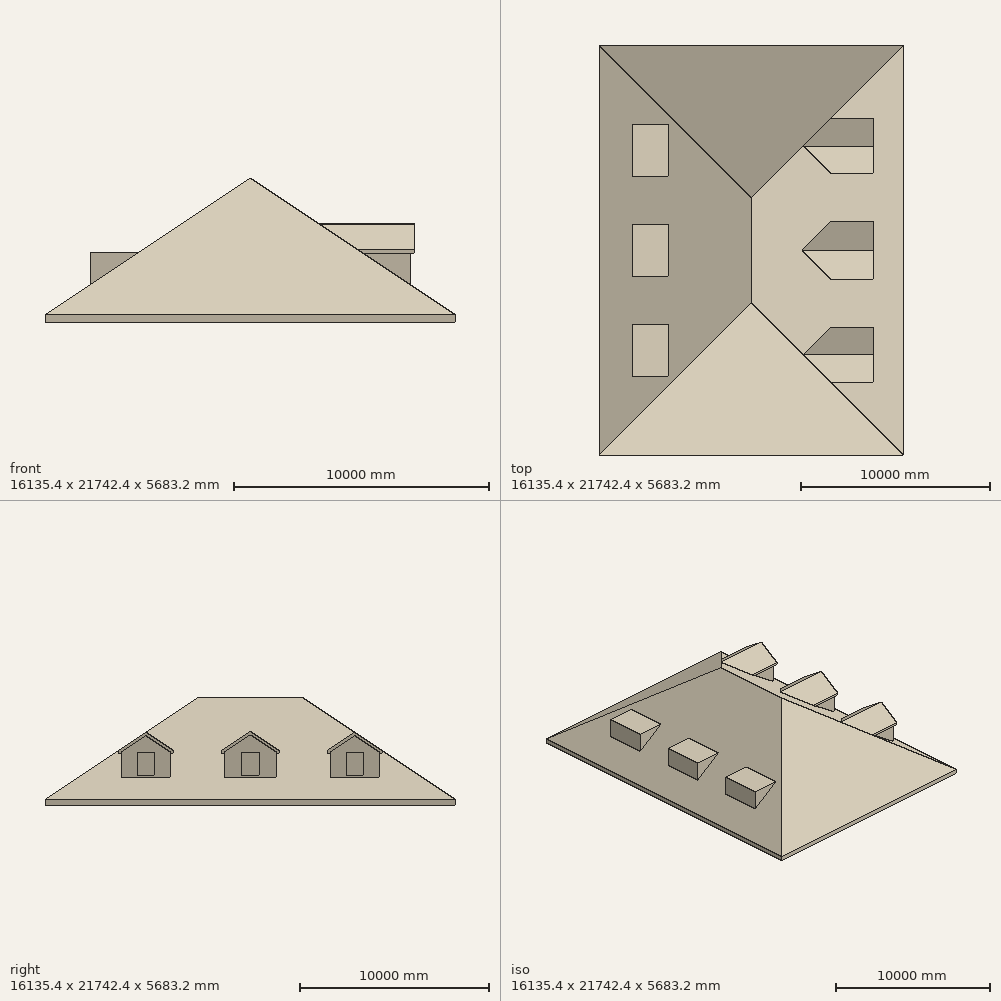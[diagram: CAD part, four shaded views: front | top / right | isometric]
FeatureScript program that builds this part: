
annotation { "Feature Type Name" : "Feature", "Feature Type Description" : "" }
export const myFeature = defineFeature(function(context is Context, id is Id, definition is map)
    precondition{}
    {
        {
            var Q0;
            Q0=qCreatedBy(makeId("Top.planeOp"),FACE);
            var sketch = newSketch(context, id + "F0", { "sketchPlane" : qUnion([Q0])});
            skLineSegment(sketch, "E0.bottom", {"start": v(0, 0) * mm, "end": v(15525.75, 0) * mm, "construction": true});
            skLineSegment(sketch, "E0.right", {"start": v(15525.75, 0) * mm, "end": v(15525.75, -21132.8) * mm, "construction": true});
            skLineSegment(sketch, "E1", {"start": v(13696.95, -21132.8) * mm, "end": v(13696.95, -22047.2) * mm, "construction": true});
            skLineSegment(sketch, "E2", {"start": v(13696.95, -22047.2) * mm, "end": v(9429.75, -22047.2) * mm, "construction": true});
            skLineSegment(sketch, "E3", {"start": v(9429.75, -22047.2) * mm, "end": v(9429.75, -21437.6) * mm, "construction": true});
            skLineSegment(sketch, "E4", {"start": v(9429.75, -21437.6) * mm, "end": v(8058.15, -21437.6) * mm, "construction": true});
            skLineSegment(sketch, "E5", {"start": v(8058.15, -21437.6) * mm, "end": v(8058.15, -21132.8) * mm, "construction": true});
            skLineSegment(sketch, "E6.trimOffspring", {"start": v(13696.95, -21132.8) * mm, "end": v(15525.75, -21132.8) * mm, "construction": true});
            skLineSegment(sketch, "E7", {"start": v(7600.95, -21132.8) * mm, "end": v(7600.95, -21590) * mm});
            skLineSegment(sketch, "E8", {"start": v(7600.95, -21590) * mm, "end": v(6838.95, -21590) * mm});
            skLineSegment(sketch, "E9", {"start": v(4019.55, -21590) * mm, "end": v(4019.55, -21132.8) * mm});
            skLineSegment(sketch, "E10.trimOffspring", {"start": v(7600.95, -21132.8) * mm, "end": v(8058.15, -21132.8) * mm, "construction": true});
            skLineSegment(sketch, "E11", {"start": v(4781.55, -21590) * mm, "end": v(4781.55, -21285.2) * mm});
            skLineSegment(sketch, "E12", {"start": v(4781.55, -21285.2) * mm, "end": v(4324.35, -21285.2) * mm});
            skLineSegment(sketch, "E13", {"start": v(4324.35, -21285.2) * mm, "end": v(4324.35, -19964.4) * mm});
            skLineSegment(sketch, "E14", {"start": v(4324.35, -19964.4) * mm, "end": v(7296.15, -19964.4) * mm});
            skLineSegment(sketch, "E15", {"start": v(7296.15, -19964.4) * mm, "end": v(7296.15, -21285.2) * mm});
            skLineSegment(sketch, "E16", {"start": v(7296.15, -21285.2) * mm, "end": v(6838.95, -21285.2) * mm});
            skLineSegment(sketch, "E17", {"start": v(6838.95, -21285.2) * mm, "end": v(6838.95, -21590) * mm});
            skLineSegment(sketch, "E18.trimOffspring", {"start": v(4781.55, -21590) * mm, "end": v(4019.55, -21590) * mm});
            skLineSegment(sketch, "E19", {"start": v(4019.55, -19659.6) * mm, "end": v(7600.95, -19659.6) * mm});
            skLineSegment(sketch, "E20", {"start": v(7600.95, -19659.6) * mm, "end": v(7600.95, -21132.8) * mm});
            skLineSegment(sketch, "E21", {"start": v(4019.55, -13868.4) * mm, "end": v(7486.65, -13868.4) * mm});
            skLineSegment(sketch, "E22", {"start": v(3905.25, -13754.1) * mm, "end": v(7486.65, -13754.1) * mm});
            skLineSegment(sketch, "E23", {"start": v(7600.95, -19659.6) * mm, "end": v(7600.95, -15201.9) * mm});
            skLineSegment(sketch, "E24", {"start": v(7486.65, -19659.6) * mm, "end": v(7486.65, -13754.1) * mm});
            skLineSegment(sketch, "E25.top", {"start": v(0, -21132.8) * mm, "end": v(4019.55, -21132.8) * mm, "construction": true});
            skLineSegment(sketch, "E25.right", {"start": v(4019.55, -13868.4) * mm, "end": v(4019.55, -21132.8) * mm});
            skLineSegment(sketch, "E26", {"start": v(0, 0) * mm, "end": v(0, -21132.8) * mm, "construction": true});
            skLineSegment(sketch, "E27", {"start": v(-304.8, -21437.6) * mm, "end": v(-304.8, 304.8) * mm});
            skLineSegment(sketch, "E28", {"start": v(-304.8, 304.8) * mm, "end": v(15830.55, 304.8) * mm});
            skLineSegment(sketch, "E29", {"start": v(15830.55, 304.8) * mm, "end": v(15830.55, -21437.6) * mm});
            skLineSegment(sketch, "E30", {"start": v(15830.55, -21437.6) * mm, "end": v(-304.8, -21437.6) * mm});
            skLineSegment(sketch, "E31.top", {"start": v(2895.6, -18237.2) * mm, "end": v(3905.25, -18237.2) * mm, "construction": true});
            skLineSegment(sketch, "E31.left", {"start": v(2895.6, -2895.6) * mm, "end": v(2895.6, -17240.25) * mm});
            skLineSegment(sketch, "E31.right", {"start": v(12630.15, -2895.6) * mm, "end": v(12630.15, -18237.2) * mm});
            skLineSegment(sketch, "E32", {"start": v(8058.15, -21437.6) * mm, "end": v(13696.95, -21437.6) * mm, "construction": true});
            skLineSegment(sketch, "E33", {"start": v(11563.35, -22047.2) * mm, "end": v(11563.35, -21437.6) * mm, "construction": true});
            skLineSegment(sketch, "E34", {"start": v(10877.55, -21437.6) * mm, "end": v(10877.55, -18237.2) * mm, "construction": true});
            skLineSegment(sketch, "E35", {"start": v(3905.25, -13754.1) * mm, "end": v(3905.25, -18237.2) * mm});
            skLineSegment(sketch, "E36", {"start": v(2895.6, -14732) * mm, "end": v(1676.4, -14732) * mm});
            skLineSegment(sketch, "E37", {"start": v(1676.4, -14732) * mm, "end": v(1676.4, -17018) * mm});
            skLineSegment(sketch, "E38", {"start": v(1676.4, -17018) * mm, "end": v(2895.6, -17018) * mm});
            skLineSegment(sketch, "E39", {"start": v(2895.6, -14509.75) * mm, "end": v(1454.15, -14509.75) * mm});
            skLineSegment(sketch, "E40", {"start": v(1454.15, -14509.75) * mm, "end": v(1454.15, -17240.25) * mm});
            skLineSegment(sketch, "E41", {"start": v(1454.15, -17240.25) * mm, "end": v(2895.6, -17240.25) * mm});
            skLineSegment(sketch, "E42", {"start": v(2895.6, -11709.4) * mm, "end": v(1676.4, -11709.4) * mm});
            skLineSegment(sketch, "E43", {"start": v(1676.4, -11709.4) * mm, "end": v(1676.4, -9423.4) * mm});
            skLineSegment(sketch, "E44", {"start": v(1676.4, -9423.4) * mm, "end": v(2895.6, -9423.4) * mm});
            skLineSegment(sketch, "E45", {"start": v(2895.6, -9201.15) * mm, "end": v(1454.15, -9201.15) * mm});
            skLineSegment(sketch, "E46", {"start": v(1454.15, -9201.15) * mm, "end": v(1454.15, -11931.65) * mm});
            skLineSegment(sketch, "E47", {"start": v(1454.15, -11931.65) * mm, "end": v(2895.6, -11931.65) * mm});
            skLineSegment(sketch, "E48", {"start": v(2895.6, -4114.8) * mm, "end": v(1676.4, -4114.8) * mm});
            skLineSegment(sketch, "E49", {"start": v(1676.4, -4114.8) * mm, "end": v(1676.4, -6400.8) * mm});
            skLineSegment(sketch, "E50", {"start": v(1676.4, -6400.8) * mm, "end": v(2895.6, -6400.8) * mm});
            skLineSegment(sketch, "E51", {"start": v(2895.6, -3892.55) * mm, "end": v(1454.15, -3892.55) * mm});
            skLineSegment(sketch, "E52", {"start": v(1454.15, -3892.55) * mm, "end": v(1454.15, -6623.05) * mm});
            skLineSegment(sketch, "E53", {"start": v(1454.15, -6623.05) * mm, "end": v(2895.6, -6623.05) * mm});
            skLineSegment(sketch, "E54", {"start": v(2895.6, -6623.05) * mm, "end": v(2895.6, -9201.15) * mm});
            skLineSegment(sketch, "E55", {"start": v(2895.6, -14509.75) * mm, "end": v(2895.6, -11931.65) * mm});
            skLineSegment(sketch, "E56", {"start": v(3505.2, -1371.6) * mm, "end": v(6045.2, -1371.6) * mm});
            skLineSegment(sketch, "E57", {"start": v(6045.2, -1371.6) * mm, "end": v(6045.2, -2895.6) * mm});
            skLineSegment(sketch, "E58", {"start": v(9480.55, -2895.6) * mm, "end": v(9480.55, -1371.6) * mm});
            skLineSegment(sketch, "E59", {"start": v(9480.55, -1371.6) * mm, "end": v(12020.55, -1371.6) * mm});
            skLineSegment(sketch, "E60", {"start": v(12020.55, -1371.6) * mm, "end": v(12020.55, -2895.6) * mm});
            skLineSegment(sketch, "E61", {"start": v(3282.95, -2895.6) * mm, "end": v(3282.95, -1149.35) * mm});
            skLineSegment(sketch, "E62", {"start": v(3282.95, -1149.35) * mm, "end": v(6267.45, -1149.35) * mm});
            skLineSegment(sketch, "E63", {"start": v(6267.45, -1149.35) * mm, "end": v(6267.45, -2895.6) * mm});
            skLineSegment(sketch, "E64", {"start": v(9258.3, -2895.6) * mm, "end": v(9258.3, -1149.35) * mm});
            skLineSegment(sketch, "E65", {"start": v(9258.3, -1149.35) * mm, "end": v(12242.8, -1149.35) * mm});
            skLineSegment(sketch, "E66", {"start": v(12242.8, -1149.35) * mm, "end": v(12242.8, -2895.6) * mm});
            skLineSegment(sketch, "E67", {"start": v(6553.2, -2895.6) * mm, "end": v(6553.2, -12649.2) * mm});
            skLineSegment(sketch, "E68", {"start": v(6667.5, -2895.6) * mm, "end": v(6667.5, -12763.5) * mm});
            skLineSegment(sketch, "E69", {"start": v(12630.15, -15036.8) * mm, "end": v(13849.35, -15036.8) * mm});
            skLineSegment(sketch, "E70", {"start": v(13849.35, -15036.8) * mm, "end": v(13849.35, -17170.4) * mm});
            skLineSegment(sketch, "E71", {"start": v(13849.35, -17170.4) * mm, "end": v(12630.15, -17170.4) * mm});
            skLineSegment(sketch, "E72", {"start": v(12630.15, -17392.65) * mm, "end": v(14071.6, -17392.65) * mm});
            skLineSegment(sketch, "E73", {"start": v(14071.6, -17392.65) * mm, "end": v(14071.6, -14814.55) * mm});
            skLineSegment(sketch, "E74", {"start": v(14071.6, -14814.55) * mm, "end": v(12630.15, -14814.55) * mm});
            skLineSegment(sketch, "E75", {"start": v(12630.15, -9423.4) * mm, "end": v(13849.35, -9423.4) * mm});
            skLineSegment(sketch, "E76", {"start": v(13849.35, -9423.4) * mm, "end": v(13849.35, -11709.4) * mm});
            skLineSegment(sketch, "E77", {"start": v(13849.35, -11709.4) * mm, "end": v(12630.15, -11709.4) * mm});
            skLineSegment(sketch, "E78", {"start": v(12630.15, -11931.65) * mm, "end": v(14071.6, -11931.65) * mm});
            skLineSegment(sketch, "E79", {"start": v(14071.6, -11931.65) * mm, "end": v(14071.6, -9201.15) * mm});
            skLineSegment(sketch, "E80", {"start": v(14071.6, -9201.15) * mm, "end": v(12630.15, -9201.15) * mm});
            skLineSegment(sketch, "E81", {"start": v(12630.15, -3962.4) * mm, "end": v(13849.35, -3962.4) * mm});
            skLineSegment(sketch, "E82", {"start": v(13849.35, -3962.4) * mm, "end": v(13849.35, -6096) * mm});
            skLineSegment(sketch, "E83", {"start": v(13849.35, -6096) * mm, "end": v(12630.15, -6096) * mm});
            skLineSegment(sketch, "E84", {"start": v(12630.15, -6318.25) * mm, "end": v(14071.6, -6318.25) * mm});
            skLineSegment(sketch, "E85", {"start": v(14071.6, -6318.25) * mm, "end": v(14071.6, -3740.15) * mm});
            skLineSegment(sketch, "E86", {"start": v(14071.6, -3740.15) * mm, "end": v(12630.15, -3740.15) * mm});
            skLineSegment(sketch, "E87", {"start": v(14071.6, -6318.25) * mm, "end": v(14071.6, -9201.15) * mm, "construction": true});
            skLineSegment(sketch, "E88", {"start": v(14071.6, -14814.55) * mm, "end": v(14071.6, -11931.65) * mm, "construction": true});
            skLineSegment(sketch, "E89", {"start": v(8934.45, -14770.1) * mm, "end": v(12630.15, -14770.1) * mm});
            skLineSegment(sketch, "E90", {"start": v(8934.45, -14884.4) * mm, "end": v(12630.15, -14884.4) * mm});
            skLineSegment(sketch, "E91", {"start": v(9721.85, -12319) * mm, "end": v(12630.15, -12319) * mm});
            skLineSegment(sketch, "E92", {"start": v(9836.15, -12433.3) * mm, "end": v(12630.15, -12433.3) * mm});
            skLineSegment(sketch, "E93", {"start": v(8820.15, -15087.6) * mm, "end": v(8820.15, -12763.5) * mm});
            skLineSegment(sketch, "E94", {"start": v(7658.1, -9156.7) * mm, "end": v(12630.15, -9156.7) * mm});
            skLineSegment(sketch, "E95", {"start": v(11817.35, -13246.1) * mm, "end": v(11817.35, -14770.1) * mm});
            skLineSegment(sketch, "E96", {"start": v(7486.65, -15087.6) * mm, "end": v(5238.75, -15087.6) * mm});
            skLineSegment(sketch, "E97", {"start": v(5238.75, -15087.6) * mm, "end": v(5238.75, -18135.6) * mm});
            skLineSegment(sketch, "E98", {"start": v(5238.75, -18135.6) * mm, "end": v(4019.55, -18135.6) * mm});
            skLineSegment(sketch, "E99", {"start": v(2895.6, -2895.6) * mm, "end": v(12630.15, -2895.6) * mm});
            skLineSegment(sketch, "E100", {"start": v(3505.2, -1371.6) * mm, "end": v(3505.2, -2895.6) * mm});
            skLineSegment(sketch, "E101", {"start": v(6267.45, -2794) * mm, "end": v(9258.3, -2794) * mm});
            skLineSegment(sketch, "E102", {"start": v(2794, -3892.55) * mm, "end": v(2794, -2794) * mm});
            skLineSegment(sketch, "E103", {"start": v(2794, -2794) * mm, "end": v(3282.95, -2794) * mm});
            skLineSegment(sketch, "E104", {"start": v(2794, -6623.05) * mm, "end": v(2794, -9201.15) * mm});
            skLineSegment(sketch, "E105", {"start": v(2794, -11931.65) * mm, "end": v(2794, -14509.75) * mm});
            skLineSegment(sketch, "E106", {"start": v(2794, -17240.25) * mm, "end": v(2794, -18338.8) * mm, "construction": true});
            skLineSegment(sketch, "E107", {"start": v(2794, -18338.8) * mm, "end": v(4019.55, -18338.8) * mm, "construction": true});
            skLineSegment(sketch, "E108", {"start": v(7600.95, -18338.8) * mm, "end": v(12731.75, -18338.8) * mm});
            skLineSegment(sketch, "E109", {"start": v(12731.75, -18338.8) * mm, "end": v(12731.75, -17392.65) * mm});
            skLineSegment(sketch, "E110", {"start": v(12731.75, -14814.55) * mm, "end": v(12731.75, -11931.65) * mm});
            skLineSegment(sketch, "E111", {"start": v(12731.75, -9201.15) * mm, "end": v(12731.75, -6318.25) * mm});
            skLineSegment(sketch, "E112", {"start": v(12242.8, -2794) * mm, "end": v(12731.75, -2794) * mm});
            skLineSegment(sketch, "E113", {"start": v(12731.75, -2794) * mm, "end": v(12731.75, -3740.15) * mm});
            skLineSegment(sketch, "E114", {"start": v(6667.5, -12763.5) * mm, "end": v(2895.6, -12763.5) * mm});
            skLineSegment(sketch, "E115", {"start": v(6553.2, -12649.2) * mm, "end": v(2895.6, -12649.2) * mm});
            skLineSegment(sketch, "E116", {"start": v(7486.65, -15087.6) * mm, "end": v(8820.15, -15087.6) * mm});
            skLineSegment(sketch, "E117", {"start": v(7600.95, -15201.9) * mm, "end": v(8934.45, -15201.9) * mm});
            skLineSegment(sketch, "E118.trimOffspring", {"start": v(8934.45, -14884.4) * mm, "end": v(8934.45, -15201.9) * mm});
            skLineSegment(sketch, "E119", {"start": v(9721.85, -12319) * mm, "end": v(9721.85, -14770.1) * mm});
            skLineSegment(sketch, "E120", {"start": v(9836.15, -12433.3) * mm, "end": v(9836.15, -14770.1) * mm});
            skLineSegment(sketch, "E121", {"start": v(10445.75, -12433.3) * mm, "end": v(10445.75, -14770.1) * mm});
            skLineSegment(sketch, "E122", {"start": v(12630.15, -13246.1) * mm, "end": v(11715.75, -13246.1) * mm});
            skLineSegment(sketch, "E123", {"start": v(11715.75, -13246.1) * mm, "end": v(11715.75, -13131.8) * mm});
            skLineSegment(sketch, "E124", {"start": v(11715.75, -13131.8) * mm, "end": v(12630.15, -13131.8) * mm});
            skLineSegment(sketch, "E125.bottom", {"start": v(12350.75, -12534.9) * mm, "end": v(12579.35, -12534.9) * mm});
            skLineSegment(sketch, "E125.top", {"start": v(12350.75, -13042.9) * mm, "end": v(12579.35, -13042.9) * mm});
            skLineSegment(sketch, "E125.left", {"start": v(12350.75, -12534.9) * mm, "end": v(12350.75, -13042.9) * mm});
            skLineSegment(sketch, "E125.right", {"start": v(12579.35, -12534.9) * mm, "end": v(12579.35, -13042.9) * mm});
            skLineSegment(sketch, "E126", {"start": v(12350.75, -12636.5) * mm, "end": v(11855.45, -12636.5) * mm});
            skLineSegment(sketch, "E127", {"start": v(11855.45, -12636.5) * mm, "end": v(11855.45, -12941.3) * mm});
            skLineSegment(sketch, "E128", {"start": v(11855.45, -12941.3) * mm, "end": v(12350.75, -12941.3) * mm});
            skLineSegment(sketch, "E129", {"start": v(11004.55, -14770.1) * mm, "end": v(11004.55, -14884.4) * mm});
            skLineSegment(sketch, "E130", {"start": v(11614.15, -14770.1) * mm, "end": v(11614.15, -14884.4) * mm});
            skLineSegment(sketch, "E131", {"start": v(11004.55, -14827.25) * mm, "end": v(11614.15, -14827.25) * mm});
            skCircle(sketch, "E132", {"center": v(10140.95, -13195.3) * mm, "radius": 165.1 * mm});
            skLineSegment(sketch, "E133", {"start": v(9836.15, -13500.1) * mm, "end": v(10445.75, -13500.1) * mm, "construction": true});
            skLineSegment(sketch, "E134", {"start": v(10445.75, -12890.5) * mm, "end": v(9836.15, -12890.5) * mm});
            skLineSegment(sketch, "E135", {"start": v(11004.55, -12319) * mm, "end": v(11004.55, -12433.3) * mm});
            skLineSegment(sketch, "E136", {"start": v(11614.15, -12319) * mm, "end": v(11614.15, -12433.3) * mm});
            skLineSegment(sketch, "E137", {"start": v(11004.55, -12376.15) * mm, "end": v(11614.15, -12376.15) * mm});
            skLineSegment(sketch, "E138.bottom", {"start": v(9112.25, -14465.3) * mm, "end": v(9620.25, -14465.3) * mm});
            skLineSegment(sketch, "E138.top", {"start": v(9112.25, -14719.3) * mm, "end": v(9620.25, -14719.3) * mm});
            skLineSegment(sketch, "E138.left", {"start": v(9112.25, -14465.3) * mm, "end": v(9112.25, -14719.3) * mm});
            skLineSegment(sketch, "E138.right", {"start": v(9620.25, -14465.3) * mm, "end": v(9620.25, -14719.3) * mm});
            skLineSegment(sketch, "E139.bottom", {"start": v(9213.85, -13970) * mm, "end": v(9518.65, -13970) * mm});
            skLineSegment(sketch, "E139.top", {"start": v(9213.85, -14465.3) * mm, "end": v(9518.65, -14465.3) * mm});
            skLineSegment(sketch, "E139.left", {"start": v(9213.85, -13970) * mm, "end": v(9213.85, -14465.3) * mm});
            skLineSegment(sketch, "E139.right", {"start": v(9518.65, -13970) * mm, "end": v(9518.65, -14465.3) * mm});
            skLineSegment(sketch, "E140", {"start": v(8934.45, -13220.7) * mm, "end": v(9721.85, -13220.7) * mm});
            skLineSegment(sketch, "E141", {"start": v(8934.45, -12763.5) * mm, "end": v(9721.85, -12763.5) * mm});
            skLineSegment(sketch, "E142", {"start": v(7702.55, -15087.6) * mm, "end": v(7702.55, -15201.9) * mm});
            skLineSegment(sketch, "E143", {"start": v(8616.95, -15087.6) * mm, "end": v(8616.95, -15201.9) * mm});
            skLineSegment(sketch, "E144", {"start": v(7702.55, -15144.75) * mm, "end": v(8616.95, -15144.75) * mm});
            skLineSegment(sketch, "E145", {"start": v(8820.15, -13322.3) * mm, "end": v(8934.45, -13322.3) * mm});
            skLineSegment(sketch, "E146", {"start": v(8820.15, -13931.9) * mm, "end": v(8934.45, -13931.9) * mm});
            skLineSegment(sketch, "E147", {"start": v(8877.3, -13931.9) * mm, "end": v(8877.3, -13322.3) * mm});
            skCircle(sketch, "E148", {"center": v(9264.65, -12992.1) * mm, "radius": 165.1 * mm});
            skLineSegment(sketch, "E149", {"start": v(7658.1, -12763.5) * mm, "end": v(8820.15, -12763.5) * mm});
            skLineSegment(sketch, "E150", {"start": v(7658.1, -12763.5) * mm, "end": v(7658.1, -9156.7) * mm});
            skLineSegment(sketch, "E151.trimOffspring", {"start": v(8934.45, -12763.5) * mm, "end": v(8934.45, -14770.1) * mm});
            skLineSegment(sketch, "E152", {"start": v(9721.85, -12649.2) * mm, "end": v(7772.4, -12649.2) * mm});
            skLineSegment(sketch, "E153", {"start": v(7772.4, -12649.2) * mm, "end": v(7772.4, -9271) * mm});
            skLineSegment(sketch, "E154", {"start": v(7772.4, -9271) * mm, "end": v(12630.15, -9271) * mm});
            skLineSegment(sketch, "E155", {"start": v(8737.6, -12763.5) * mm, "end": v(8737.6, -12649.2) * mm});
            skLineSegment(sketch, "E156", {"start": v(7874, -12763.5) * mm, "end": v(7874, -12649.2) * mm});
            skLineSegment(sketch, "E157", {"start": v(7874, -12706.35) * mm, "end": v(8737.6, -12706.35) * mm});
            skLineSegment(sketch, "E158", {"start": v(7772.4, -11734.8) * mm, "end": v(8496.3, -11734.8) * mm});
            skLineSegment(sketch, "E159", {"start": v(9105.9, -11125.2) * mm, "end": v(9105.9, -9271) * mm});
            skLineSegment(sketch, "E160", {"start": v(7772.4, -11620.5) * mm, "end": v(8448.96, -11620.5) * mm});
            skLineSegment(sketch, "E161", {"start": v(8991.6, -11077.86) * mm, "end": v(8991.6, -9271) * mm});
            skLineSegment(sketch, "E162", {"start": v(8280.4, -9271) * mm, "end": v(8280.4, -11620.5) * mm});
            skLineSegment(sketch, "E163", {"start": v(5334, -12649.2) * mm, "end": v(5334, -6553.2) * mm, "construction": true});
            skLineSegment(sketch, "E164", {"start": v(5334, -6553.2) * mm, "end": v(6667.5, -6553.2) * mm, "construction": true});
            skLineSegment(sketch, "E165", {"start": v(2895.6, -17018) * mm, "end": v(3905.25, -17018) * mm});
            skLineSegment(sketch, "E166", {"start": v(2895.6, -17132.3) * mm, "end": v(3905.25, -17132.3) * mm});
            skLineSegment(sketch, "E167", {"start": v(8991.6, -9779) * mm, "end": v(8280.4, -9779) * mm});
            skLineSegment(sketch, "E168", {"start": v(8448.96, -11620.5) * mm, "end": v(8991.6, -11077.86) * mm});
            skLineSegment(sketch, "E169", {"start": v(8496.3, -11734.8) * mm, "end": v(9105.9, -11125.2) * mm});
            skLineSegment(sketch, "E170", {"start": v(8515.65, -11553.8) * mm, "end": v(8596.47, -11634.63) * mm});
            skLineSegment(sketch, "E171", {"start": v(8946.7, -11122.76) * mm, "end": v(9027.52, -11203.58) * mm});
            skLineSegment(sketch, "E172", {"start": v(8556.06, -11594.22) * mm, "end": v(8987.1, -11163.17) * mm});
            skLineSegment(sketch, "E173", {"start": v(6667.5, -8699.5) * mm, "end": v(7658.1, -8699.5) * mm});
            skLineSegment(sketch, "E174", {"start": v(6667.5, -8813.8) * mm, "end": v(7658.1, -8813.8) * mm});
            skLineSegment(sketch, "E175", {"start": v(6731, -8699.5) * mm, "end": v(6731, -8813.8) * mm});
            skLineSegment(sketch, "E176", {"start": v(7594.6, -8699.5) * mm, "end": v(7594.6, -8813.8) * mm});
            skLineSegment(sketch, "E177", {"start": v(6731, -8756.65) * mm, "end": v(7594.6, -8756.65) * mm});
            skLineSegment(sketch, "E178", {"start": v(13849.35, -15570.2) * mm, "end": v(14071.6, -15570.2) * mm});
            skLineSegment(sketch, "E179", {"start": v(13849.35, -16789.4) * mm, "end": v(14071.6, -16789.4) * mm});
            skLineSegment(sketch, "E180", {"start": v(13960.47, -16789.4) * mm, "end": v(13960.47, -15570.2) * mm});
            skLineSegment(sketch, "E181", {"start": v(13849.35, -9956.8) * mm, "end": v(14071.6, -9956.8) * mm});
            skLineSegment(sketch, "E182", {"start": v(13849.35, -11176) * mm, "end": v(14071.6, -11176) * mm});
            skLineSegment(sketch, "E183", {"start": v(13960.47, -11176) * mm, "end": v(13960.47, -9956.8) * mm});
            skLineSegment(sketch, "E184", {"start": v(13849.35, -4343.4) * mm, "end": v(14071.6, -4343.4) * mm});
            skLineSegment(sketch, "E185", {"start": v(13849.35, -5562.6) * mm, "end": v(14071.6, -5562.6) * mm});
            skLineSegment(sketch, "E186", {"start": v(13960.47, -4343.4) * mm, "end": v(13960.47, -5562.6) * mm});
            skLineSegment(sketch, "E187", {"start": v(9734.55, -1149.35) * mm, "end": v(9734.55, -1371.6) * mm});
            skLineSegment(sketch, "E188", {"start": v(10648.95, -1149.35) * mm, "end": v(10648.95, -1371.6) * mm});
            skLineSegment(sketch, "E189", {"start": v(9734.55, -1260.47) * mm, "end": v(10648.95, -1260.47) * mm});
            skLineSegment(sketch, "E190", {"start": v(10852.15, -1149.35) * mm, "end": v(10852.15, -1371.6) * mm});
            skLineSegment(sketch, "E191", {"start": v(11766.55, -1149.35) * mm, "end": v(11766.55, -1371.6) * mm});
            skLineSegment(sketch, "E192", {"start": v(10852.15, -1260.47) * mm, "end": v(11766.55, -1260.47) * mm});
            skLineSegment(sketch, "E193", {"start": v(3759.2, -1371.6) * mm, "end": v(3759.2, -1149.35) * mm});
            skLineSegment(sketch, "E194", {"start": v(4673.6, -1371.6) * mm, "end": v(4673.6, -1149.35) * mm});
            skLineSegment(sketch, "E195", {"start": v(4876.8, -1371.6) * mm, "end": v(4876.8, -1149.35) * mm});
            skLineSegment(sketch, "E196", {"start": v(5791.2, -1371.6) * mm, "end": v(5791.2, -1149.35) * mm});
            skLineSegment(sketch, "E197", {"start": v(3759.2, -1260.47) * mm, "end": v(4673.6, -1260.47) * mm});
            skLineSegment(sketch, "E198", {"start": v(4876.8, -1260.47) * mm, "end": v(5791.2, -1260.47) * mm});
            skLineSegment(sketch, "E199", {"start": v(1454.15, -5867.4) * mm, "end": v(1676.4, -5867.4) * mm});
            skLineSegment(sketch, "E200", {"start": v(1454.15, -4648.2) * mm, "end": v(1676.4, -4648.2) * mm});
            skLineSegment(sketch, "E201", {"start": v(1565.27, -5867.4) * mm, "end": v(1565.27, -4648.2) * mm});
            skLineSegment(sketch, "E202", {"start": v(1454.15, -9956.8) * mm, "end": v(1676.4, -9956.8) * mm});
            skLineSegment(sketch, "E203", {"start": v(1454.15, -11176) * mm, "end": v(1676.4, -11176) * mm});
            skLineSegment(sketch, "E204", {"start": v(1565.27, -11176) * mm, "end": v(1565.27, -9956.8) * mm});
            skLineSegment(sketch, "E205", {"start": v(2895.6, -17240.25) * mm, "end": v(2895.6, -18237.2) * mm, "construction": true});
            skLineSegment(sketch, "E206", {"start": v(3905.25, -18237.2) * mm, "end": v(12630.15, -18237.2) * mm});
            skLineSegment(sketch, "E207", {"start": v(1454.15, -15265.4) * mm, "end": v(1676.4, -15265.4) * mm});
            skLineSegment(sketch, "E208", {"start": v(1454.15, -16484.6) * mm, "end": v(1676.4, -16484.6) * mm});
            skLineSegment(sketch, "E209", {"start": v(1565.27, -16484.6) * mm, "end": v(1565.27, -15265.4) * mm});
            skLineSegment(sketch, "E210", {"start": v(9734.55, -18338.8) * mm, "end": v(9734.55, -21437.6) * mm});
            skLineSegment(sketch, "E211", {"start": v(9620.25, -18338.8) * mm, "end": v(9620.25, -21437.6) * mm});
            skLineSegment(sketch, "E212", {"start": v(12020.55, -18338.8) * mm, "end": v(12020.55, -21437.6) * mm});
            skLineSegment(sketch, "E213", {"start": v(12134.85, -18338.8) * mm, "end": v(12134.85, -21437.6) * mm});
            skLineSegment(sketch, "E214", {"start": v(10242.55, -18338.8) * mm, "end": v(10242.55, -21437.6) * mm});
            skLineSegment(sketch, "E215", {"start": v(11512.55, -18338.8) * mm, "end": v(11512.55, -21437.6) * mm});
            skLineSegment(sketch, "E216", {"start": v(10572.75, -18237.2) * mm, "end": v(10572.75, -18338.8) * mm});
            skLineSegment(sketch, "E217", {"start": v(11182.35, -18237.2) * mm, "end": v(11182.35, -18338.8) * mm});
            skLineSegment(sketch, "E218", {"start": v(10572.75, -18288) * mm, "end": v(11182.35, -18288) * mm});
            skLineSegment(sketch, "E219", {"start": v(7658.1, -9156.7) * mm, "end": v(7658.1, -6096) * mm});
            skLineSegment(sketch, "E220", {"start": v(7658.1, -6096) * mm, "end": v(12630.15, -6096) * mm});
            skLineSegment(sketch, "E221", {"start": v(7772.4, -9156.7) * mm, "end": v(7772.4, -6210.3) * mm});
            skLineSegment(sketch, "E222", {"start": v(7772.4, -6210.3) * mm, "end": v(12630.15, -6210.3) * mm});
            skLineSegment(sketch, "E223", {"start": v(9601.2, -9156.7) * mm, "end": v(9601.2, -8293.1) * mm});
            skLineSegment(sketch, "E224", {"start": v(9601.2, -8293.1) * mm, "end": v(9715.5, -8293.1) * mm});
            skLineSegment(sketch, "E225", {"start": v(9715.5, -8293.1) * mm, "end": v(9715.5, -9156.7) * mm});
            skLineSegment(sketch, "E226", {"start": v(7772.4, -8547.1) * mm, "end": v(9601.2, -8547.1) * mm});
            skLineSegment(sketch, "E227", {"start": v(9144, -8547.1) * mm, "end": v(9144, -9156.7) * mm});
            skCircle(sketch, "E228", {"center": v(8458.2, -8851.9) * mm, "radius": 165.1 * mm});
            skLineSegment(sketch, "E229.bottom", {"start": v(9817.1, -8877.3) * mm, "end": v(10325.1, -8877.3) * mm});
            skLineSegment(sketch, "E229.top", {"start": v(9817.1, -9105.9) * mm, "end": v(10325.1, -9105.9) * mm});
            skLineSegment(sketch, "E229.left", {"start": v(9817.1, -8877.3) * mm, "end": v(9817.1, -9105.9) * mm});
            skLineSegment(sketch, "E229.right", {"start": v(10325.1, -8877.3) * mm, "end": v(10325.1, -9105.9) * mm});
            skLineSegment(sketch, "E230", {"start": v(9918.7, -8877.3) * mm, "end": v(9918.7, -8382) * mm});
            skLineSegment(sketch, "E231", {"start": v(9918.7, -8382) * mm, "end": v(10223.5, -8382) * mm});
            skLineSegment(sketch, "E232", {"start": v(10223.5, -8382) * mm, "end": v(10223.5, -8877.3) * mm});
            skLineSegment(sketch, "E233", {"start": v(9677.4, -6210.3) * mm, "end": v(9677.4, -7543.8) * mm});
            skLineSegment(sketch, "E234", {"start": v(9677.4, -7543.8) * mm, "end": v(11125.2, -7543.8) * mm});
            skLineSegment(sketch, "E235", {"start": v(11125.2, -7543.8) * mm, "end": v(11125.2, -6210.3) * mm});
            skLineSegment(sketch, "E236", {"start": v(9677.4, -7429.5) * mm, "end": v(7772.4, -7429.5) * mm});
            skLineSegment(sketch, "E237", {"start": v(9791.7, -6210.3) * mm, "end": v(9791.7, -7429.5) * mm});
            skLineSegment(sketch, "E238", {"start": v(9791.7, -7429.5) * mm, "end": v(11010.9, -7429.5) * mm});
            skLineSegment(sketch, "E239", {"start": v(11010.9, -7429.5) * mm, "end": v(11010.9, -6210.3) * mm});
            skLineSegment(sketch, "E240", {"start": v(9791.7, -7429.5) * mm, "end": v(11010.9, -6210.3) * mm});
            skLineSegment(sketch, "E241", {"start": v(11010.9, -7429.5) * mm, "end": v(9791.7, -6210.3) * mm});
            skLineSegment(sketch, "E242.bottom", {"start": v(7899.4, -6337.3) * mm, "end": v(9550.4, -6337.3) * mm});
            skLineSegment(sketch, "E242.top", {"start": v(7899.4, -7302.5) * mm, "end": v(9550.4, -7302.5) * mm});
            skLineSegment(sketch, "E242.left", {"start": v(7899.4, -6337.3) * mm, "end": v(7899.4, -7302.5) * mm});
            skLineSegment(sketch, "E242.right", {"start": v(9550.4, -6337.3) * mm, "end": v(9550.4, -7302.5) * mm});
            skLineSegment(sketch, "E243", {"start": v(10426.7, -9156.7) * mm, "end": v(10426.7, -7543.8) * mm});
            skLineSegment(sketch, "E244", {"start": v(10541, -9156.7) * mm, "end": v(10541, -7543.8) * mm});
            skLineSegment(sketch, "E245", {"start": v(10426.7, -7645.4) * mm, "end": v(10541, -7645.4) * mm});
            skLineSegment(sketch, "E246", {"start": v(10426.7, -8255) * mm, "end": v(10541, -8255) * mm});
            skLineSegment(sketch, "E247", {"start": v(10483.85, -8255) * mm, "end": v(10483.85, -7645.4) * mm});
            skLineSegment(sketch, "E248", {"start": v(9842.5, -7429.5) * mm, "end": v(9842.5, -7543.8) * mm});
            skLineSegment(sketch, "E249", {"start": v(10375.9, -7429.5) * mm, "end": v(10375.9, -7543.8) * mm});
            skLineSegment(sketch, "E250", {"start": v(9842.5, -7486.65) * mm, "end": v(10375.9, -7486.65) * mm});
            skLineSegment(sketch, "E251", {"start": v(10541, -8648.7) * mm, "end": v(12122.15, -8648.7) * mm});
            skLineSegment(sketch, "E252", {"start": v(12122.15, -8648.7) * mm, "end": v(12122.15, -6718.3) * mm});
            skLineSegment(sketch, "E253", {"start": v(12122.15, -6718.3) * mm, "end": v(11125.2, -6718.3) * mm});
            skLineSegment(sketch, "E254", {"start": v(7658.1, -7683.5) * mm, "end": v(7772.4, -7683.5) * mm});
            skLineSegment(sketch, "E255", {"start": v(7658.1, -8293.1) * mm, "end": v(7772.4, -8293.1) * mm});
            skLineSegment(sketch, "E256", {"start": v(7715.25, -8293.1) * mm, "end": v(7715.25, -7683.5) * mm});
            skLineSegment(sketch, "E257", {"start": v(4838.7, -11925.3) * mm, "end": v(4838.7, -12649.2) * mm});
            skLineSegment(sketch, "E258", {"start": v(2895.6, -12039.6) * mm, "end": v(4724.4, -12039.6) * mm});
            skLineSegment(sketch, "E259", {"start": v(4724.4, -12039.6) * mm, "end": v(4724.4, -12649.2) * mm});
            skLineSegment(sketch, "E260", {"start": v(6553.2, -8775.7) * mm, "end": v(5829.3, -8775.7) * mm});
            skLineSegment(sketch, "E261", {"start": v(5829.3, -8775.7) * mm, "end": v(5829.3, -12649.2) * mm});
            skLineSegment(sketch, "E262", {"start": v(6553.2, -8890) * mm, "end": v(5943.6, -8890) * mm});
            skLineSegment(sketch, "E263", {"start": v(5943.6, -8890) * mm, "end": v(5943.6, -12649.2) * mm});
            skLineSegment(sketch, "E264", {"start": v(4838.7, -11925.3) * mm, "end": v(2895.6, -11925.3) * mm});
            skLineSegment(sketch, "E265", {"start": v(4902.2, -12649.2) * mm, "end": v(4902.2, -12763.5) * mm});
            skLineSegment(sketch, "E266", {"start": v(5765.8, -12649.2) * mm, "end": v(5765.8, -12763.5) * mm});
            skLineSegment(sketch, "E267", {"start": v(4902.2, -12706.35) * mm, "end": v(5765.8, -12706.35) * mm});
            skLineSegment(sketch, "E268", {"start": v(2997.2, -11925.3) * mm, "end": v(2997.2, -12039.6) * mm});
            skLineSegment(sketch, "E269", {"start": v(4622.8, -11925.3) * mm, "end": v(4622.8, -12039.6) * mm});
            skLineSegment(sketch, "E270", {"start": v(2997.2, -11982.45) * mm, "end": v(4622.8, -11982.45) * mm});
            skLineSegment(sketch, "E271", {"start": v(6553.2, -12547.6) * mm, "end": v(6667.5, -12547.6) * mm});
            skLineSegment(sketch, "E272", {"start": v(6553.2, -10922) * mm, "end": v(6667.5, -10922) * mm});
            skLineSegment(sketch, "E273", {"start": v(6610.35, -12547.6) * mm, "end": v(6610.35, -10922) * mm});
            skLineSegment(sketch, "E274", {"start": v(5943.6, -10820.4) * mm, "end": v(6553.2, -10820.4) * mm});
            skLineSegment(sketch, "E275", {"start": v(5943.6, -10706.1) * mm, "end": v(6553.2, -10706.1) * mm});
            skLineSegment(sketch, "E276", {"start": v(5829.3, -10617.2) * mm, "end": v(5943.6, -10617.2) * mm});
            skLineSegment(sketch, "E277", {"start": v(5829.3, -8991.6) * mm, "end": v(5943.6, -8991.6) * mm});
            skLineSegment(sketch, "E278", {"start": v(5886.45, -8991.6) * mm, "end": v(5886.45, -10617.2) * mm});
            skLineSegment(sketch, "E279", {"start": v(6667.5, -3302) * mm, "end": v(8902.7, -3302) * mm});
            skLineSegment(sketch, "E280", {"start": v(8902.7, -3302) * mm, "end": v(8902.7, -5334) * mm});
            skLineSegment(sketch, "E281", {"start": v(8902.7, -5334) * mm, "end": v(6667.5, -5334) * mm});
            skLineSegment(sketch, "E282", {"start": v(8902.7, -3810) * mm, "end": v(9309.1, -3810) * mm});
            skLineSegment(sketch, "E283", {"start": v(9309.1, -3810) * mm, "end": v(9309.1, -4826) * mm});
            skLineSegment(sketch, "E284", {"start": v(9309.1, -4826) * mm, "end": v(8902.7, -4826) * mm});
            skLineSegment(sketch, "E285", {"start": v(10623.55, -6096) * mm, "end": v(10623.55, -5410.2) * mm});
            skLineSegment(sketch, "E286", {"start": v(10623.55, -5410.2) * mm, "end": v(12020.55, -5410.2) * mm});
            skLineSegment(sketch, "E287", {"start": v(12020.55, -5410.2) * mm, "end": v(12020.55, -6096) * mm});
            skSolve(sketch);
        }
        {
            var Q0;
            {var subQ0=sQuery(id+"F0.wireOp",EDGE,"E239");Q0=makeQuery(id+"F0.imprint","IMPRINT",FACE,{"disambiguationData":[TD([[makeQuery(id+"F0.imprint","IMPRINT",EDGE,{"derivedFrom":subQ0}),1.0]])]});}
            var Q1;
            {var subQ6=sQuery(id+"F0.wireOp",EDGE,"E81");Q1=makeQuery(id+"F0.imprint","IMPRINT",FACE,{"disambiguationData":[TD([[makeQuery(id+"F0.imprint","IMPRINT",EDGE,{"derivedFrom":subQ6}),1.0]])]});}
            var Q2;
            {var subQ4=sQuery(id+"F0.wireOp",EDGE,"E274");Q2=makeQuery(id+"F0.imprint","IMPRINT",FACE,{"disambiguationData":[TD([[makeQuery(id+"F0.imprint","IMPRINT",EDGE,{"derivedFrom":subQ4}),-1.0]])]});}
            var Q3;
            {var subQ0=sQuery(id+"F0.wireOp",EDGE,"E42");Q3=makeQuery(id+"F0.imprint","IMPRINT",FACE,{"disambiguationData":[TD([[makeQuery(id+"F0.imprint","IMPRINT",EDGE,{"derivedFrom":subQ0}),1.0]])]});}
            var Q4;
            {var subQ3=sQuery(id+"F0.wireOp",EDGE,"E96");Q4=makeQuery(id+"F0.imprint","IMPRINT",FACE,{"disambiguationData":[TD([[makeQuery(id+"F0.imprint","IMPRINT",EDGE,{"derivedFrom":subQ3}),1.0]])]});}
            var Q5;
            {var subQ0=sQuery(id+"F0.wireOp",EDGE,"E75");Q5=makeQuery(id+"F0.imprint","IMPRINT",FACE,{"disambiguationData":[TD([[makeQuery(id+"F0.imprint","IMPRINT",EDGE,{"derivedFrom":subQ0}),1.0]])]});}
            var Q6;
            {var subQ0=sQuery(id+"F0.wireOp",EDGE,"E57");Q6=makeQuery(id+"F0.imprint","IMPRINT",FACE,{"disambiguationData":[TD([[makeQuery(id+"F0.imprint","IMPRINT",EDGE,{"derivedFrom":subQ0}),-1.0]])]});}
            var Q7;
            {var subQ3=sQuery(id+"F0.wireOp",EDGE,"E227");Q7=makeQuery(id+"F0.imprint","IMPRINT",FACE,{"disambiguationData":[TD([[makeQuery(id+"F0.imprint","IMPRINT",EDGE,{"derivedFrom":subQ3}),-1.0]])]});}
            var Q8;
            {var subQ0=sQuery(id+"F0.wireOp",EDGE,"E118.trimOffspring");Q8=makeQuery(id+"F0.imprint","IMPRINT",FACE,{"disambiguationData":[TD([[makeQuery(id+"F0.imprint","IMPRINT",EDGE,{"derivedFrom":subQ0}),1.0]])]});}
            var Q9;
            {var subQ1=sQuery(id+"F0.wireOp",EDGE,"E20");Q9=makeQuery(id+"F0.imprint","IMPRINT",FACE,{"disambiguationData":[TD([[makeQuery(id+"F0.imprint","IMPRINT",EDGE,{"derivedFrom":subQ1}),1.0]])]});}
            var Q10;
            {var subQ4=sQuery(id+"F0.wireOp",EDGE,"E77");Q10=makeQuery(id+"F0.imprint","IMPRINT",FACE,{"disambiguationData":[TD([[makeQuery(id+"F0.imprint","IMPRINT",EDGE,{"derivedFrom":subQ4}),1.0]])]});}
            var Q11;
            {var subQ0=sQuery(id+"F0.wireOp",EDGE,"E83");Q11=makeQuery(id+"F0.imprint","IMPRINT",FACE,{"disambiguationData":[TD([[makeQuery(id+"F0.imprint","IMPRINT",EDGE,{"derivedFrom":subQ0}),1.0]])]});}
            var Q12;
            {var subQ8=sQuery(id+"F0.wireOp",EDGE,"E100");Q12=makeQuery(id+"F0.imprint","IMPRINT",FACE,{"disambiguationData":[TD([[makeQuery(id+"F0.imprint","IMPRINT",EDGE,{"derivedFrom":subQ8}),-1.0]])]});}
            var Q13;
            {var subQ0=sQuery(id+"F0.wireOp",EDGE,"E25.right");var subQ1=sQuery(id+"F0.wireOp",EDGE,"E19");var subQ2=makeQuery(id+"F0.imprint","INTERSECT",VERTEX,{"derivedFrom":[subQ1,subQ0]});Q13=makeQuery(id+"F0.imprint","IMPRINT",FACE,{"disambiguationData":[TD([[makeQuery(id+"F0.imprint","IMPRINT",EDGE,{"disambiguationData":[TD([[subQ2,-1.0]])],"derivedFrom":subQ1}),1.0]])]});}
            var Q14;
            {var subQ4=sQuery(id+"F0.wireOp",EDGE,"E71");Q14=makeQuery(id+"F0.imprint","IMPRINT",FACE,{"disambiguationData":[TD([[makeQuery(id+"F0.imprint","IMPRINT",EDGE,{"derivedFrom":subQ4}),1.0]])]});}
            var Q15;
            Q15=makeQuery(id+"F0.imprint","IMPRINT",FACE,{"disambiguationData":[TD([[makeQuery(id+"F0.imprint","IMPRINT",EDGE,{"derivedFrom":sQuery(id+"F0.wireOp",EDGE,"E132")}),-1.0]])]});
            var Q16;
            {var subQ10=sQuery(id+"F0.wireOp",EDGE,"E251");Q16=makeQuery(id+"F0.imprint","IMPRINT",FACE,{"disambiguationData":[TD([[makeQuery(id+"F0.imprint","IMPRINT",EDGE,{"derivedFrom":subQ10}),-1.0]])]});}
            var Q17;
            {var subQ5=sQuery(id+"F0.wireOp",EDGE,"E167");Q17=makeQuery(id+"F0.imprint","IMPRINT",FACE,{"disambiguationData":[TD([[makeQuery(id+"F0.imprint","IMPRINT",EDGE,{"derivedFrom":subQ5}),-1.0]])]});}
            var Q18;
            {var subQ4=sQuery(id+"F0.wireOp",EDGE,"E42");Q18=makeQuery(id+"F0.imprint","IMPRINT",FACE,{"disambiguationData":[TD([[makeQuery(id+"F0.imprint","IMPRINT",EDGE,{"derivedFrom":subQ4}),-1.0]])]});}
            var Q19;
            {var subQ8=sQuery(id+"F0.wireOp",EDGE,"E57");Q19=makeQuery(id+"F0.imprint","IMPRINT",FACE,{"disambiguationData":[TD([[makeQuery(id+"F0.imprint","IMPRINT",EDGE,{"derivedFrom":subQ8}),1.0]])]});}
            var Q20;
            {var subQ0=sQuery(id+"F0.wireOp",EDGE,"E212");Q20=makeQuery(id+"F0.imprint","IMPRINT",FACE,{"disambiguationData":[TD([[makeQuery(id+"F0.imprint","IMPRINT",EDGE,{"derivedFrom":subQ0}),-1.0]])]});}
            var Q21;
            {var subQ1=sQuery(id+"F0.wireOp",EDGE,"E36");Q21=makeQuery(id+"F0.imprint","IMPRINT",FACE,{"disambiguationData":[TD([[makeQuery(id+"F0.imprint","IMPRINT",EDGE,{"derivedFrom":subQ1}),1.0]])]});}
            var Q22;
            {var subQ6=sQuery(id+"F0.wireOp",EDGE,"E58");Q22=makeQuery(id+"F0.imprint","IMPRINT",FACE,{"disambiguationData":[TD([[makeQuery(id+"F0.imprint","IMPRINT",EDGE,{"derivedFrom":subQ6}),-1.0]])]});}
            var Q23;
            {var subQ9=sQuery(id+"F0.wireOp",EDGE,"E158");Q23=makeQuery(id+"F0.imprint","IMPRINT",FACE,{"disambiguationData":[TD([[makeQuery(id+"F0.imprint","IMPRINT",EDGE,{"derivedFrom":subQ9}),-1.0]])]});}
            var Q24;
            {var subQ0=sQuery(id+"F0.wireOp",EDGE,"E210");Q24=makeQuery(id+"F0.imprint","IMPRINT",FACE,{"disambiguationData":[TD([[makeQuery(id+"F0.imprint","IMPRINT",EDGE,{"derivedFrom":subQ0}),1.0]])]});}
            var Q25;
            Q25=makeQuery(id+"F0.imprint","IMPRINT",FACE,{"disambiguationData":[TD([[makeQuery(id+"F0.imprint","IMPRINT",EDGE,{"derivedFrom":sQuery(id+"F0.wireOp",EDGE,"E138.top")}),-1.0]])]});
            var Q26;
            {var subQ11=sQuery(id+"F0.wireOp",EDGE,"E58");Q26=makeQuery(id+"F0.imprint","IMPRINT",FACE,{"disambiguationData":[TD([[makeQuery(id+"F0.imprint","IMPRINT",EDGE,{"derivedFrom":subQ11}),1.0]])]});}
            var Q27;
            {var subQ2=sQuery(id+"F0.wireOp",EDGE,"E251");Q27=makeQuery(id+"F0.imprint","IMPRINT",FACE,{"disambiguationData":[TD([[makeQuery(id+"F0.imprint","IMPRINT",EDGE,{"derivedFrom":subQ2}),1.0]])]});}
            var Q28;
            {var subQ12=sQuery(id+"F0.wireOp",EDGE,"E95");Q28=makeQuery(id+"F0.imprint","IMPRINT",FACE,{"disambiguationData":[TD([[makeQuery(id+"F0.imprint","IMPRINT",EDGE,{"derivedFrom":subQ12}),-1.0]])]});}
            var Q29;
            {var subQ1=sQuery(id+"F0.wireOp",EDGE,"E238");var subQ4=makeQuery(id+"F0.imprint","INTERSECT",VERTEX,{"derivedFrom":[subQ1,sQuery(id+"F0.wireOp",EDGE,"E249")]});Q29=makeQuery(id+"F0.imprint","IMPRINT",FACE,{"disambiguationData":[TD([[makeQuery(id+"F0.imprint","IMPRINT",EDGE,{"disambiguationData":[TD([[subQ4,1.0]])],"derivedFrom":subQ1}),1.0]])]});}
            var Q30;
            {var subQ3=sQuery(id+"F0.wireOp",EDGE,"E214");Q30=makeQuery(id+"F0.imprint","IMPRINT",FACE,{"disambiguationData":[TD([[makeQuery(id+"F0.imprint","IMPRINT",EDGE,{"derivedFrom":subQ3}),1.0]])]});}
            var Q31;
            {var subQ26=sQuery(id+"F0.wireOp",EDGE,"E224");Q31=makeQuery(id+"F0.imprint","IMPRINT",FACE,{"disambiguationData":[TD([[makeQuery(id+"F0.imprint","IMPRINT",EDGE,{"derivedFrom":subQ26}),1.0]])]});}
            var Q32;
            {var subQ4=sQuery(id+"F0.wireOp",EDGE,"E81");Q32=makeQuery(id+"F0.imprint","IMPRINT",FACE,{"disambiguationData":[TD([[makeQuery(id+"F0.imprint","IMPRINT",EDGE,{"derivedFrom":subQ4}),-1.0]])]});}
            var Q33;
            {var subQ5=sQuery(id+"F0.wireOp",EDGE,"E60");Q33=makeQuery(id+"F0.imprint","IMPRINT",FACE,{"disambiguationData":[TD([[makeQuery(id+"F0.imprint","IMPRINT",EDGE,{"derivedFrom":subQ5}),1.0]])]});}
            var Q34;
            {var subQ0=sQuery(id+"F0.wireOp",EDGE,"E38");Q34=makeQuery(id+"F0.imprint","IMPRINT",FACE,{"disambiguationData":[TD([[makeQuery(id+"F0.imprint","IMPRINT",EDGE,{"derivedFrom":subQ0}),-1.0]])]});}
            var Q35;
            {var subQ3=sQuery(id+"F0.wireOp",EDGE,"E279");Q35=makeQuery(id+"F0.imprint","IMPRINT",FACE,{"disambiguationData":[TD([[makeQuery(id+"F0.imprint","IMPRINT",EDGE,{"derivedFrom":subQ3}),1.0]])]});}
            var Q36;
            {var subQ1=sQuery(id+"F0.wireOp",EDGE,"E279");Q36=makeQuery(id+"F0.imprint","IMPRINT",FACE,{"disambiguationData":[TD([[makeQuery(id+"F0.imprint","IMPRINT",EDGE,{"derivedFrom":subQ1}),-1.0]])]});}
            var Q37;
            {var subQ3=sQuery(id+"F0.wireOp",EDGE,"E227");Q37=makeQuery(id+"F0.imprint","IMPRINT",FACE,{"disambiguationData":[TD([[makeQuery(id+"F0.imprint","IMPRINT",EDGE,{"derivedFrom":subQ3}),1.0]])]});}
            var Q38;
            {var subQ1=sQuery(id+"F0.wireOp",EDGE,"E75");Q38=makeQuery(id+"F0.imprint","IMPRINT",FACE,{"disambiguationData":[TD([[makeQuery(id+"F0.imprint","IMPRINT",EDGE,{"derivedFrom":subQ1}),-1.0]])]});}
            var Q39;
            {var subQ4=sQuery(id+"F0.wireOp",EDGE,"E48");Q39=makeQuery(id+"F0.imprint","IMPRINT",FACE,{"disambiguationData":[TD([[makeQuery(id+"F0.imprint","IMPRINT",EDGE,{"derivedFrom":subQ4}),-1.0]])]});}
            var Q40;
            {var subQ7=sQuery(id+"F0.wireOp",EDGE,"E50");Q40=makeQuery(id+"F0.imprint","IMPRINT",FACE,{"disambiguationData":[TD([[makeQuery(id+"F0.imprint","IMPRINT",EDGE,{"derivedFrom":subQ7}),-1.0]])]});}
            var Q41;
            {var subQ24=sQuery(id+"F0.wireOp",EDGE,"E22");Q41=makeQuery(id+"F0.imprint","IMPRINT",FACE,{"disambiguationData":[TD([[makeQuery(id+"F0.imprint","IMPRINT",EDGE,{"derivedFrom":subQ24}),1.0]])]});}
            var Q42;
            {var subQ5=sQuery(id+"F0.wireOp",EDGE,"E95");Q42=makeQuery(id+"F0.imprint","IMPRINT",FACE,{"disambiguationData":[TD([[makeQuery(id+"F0.imprint","IMPRINT",EDGE,{"derivedFrom":subQ5}),1.0]])]});}
            var Q43;
            {var subQ5=sQuery(id+"F0.wireOp",EDGE,"E134");Q43=makeQuery(id+"F0.imprint","IMPRINT",FACE,{"disambiguationData":[TD([[makeQuery(id+"F0.imprint","IMPRINT",EDGE,{"derivedFrom":subQ5}),-1.0]])]});}
            var Q44;
            {var subQ2=sQuery(id+"F0.wireOp",EDGE,"E21");Q44=makeQuery(id+"F0.imprint","IMPRINT",FACE,{"disambiguationData":[TD([[makeQuery(id+"F0.imprint","IMPRINT",EDGE,{"derivedFrom":subQ2}),-1.0]])]});}
            var Q45;
            {var subQ0=sQuery(id+"F0.wireOp",EDGE,"E282");Q45=makeQuery(id+"F0.imprint","IMPRINT",FACE,{"disambiguationData":[TD([[makeQuery(id+"F0.imprint","IMPRINT",EDGE,{"derivedFrom":subQ0}),-1.0]])]});}
            var Q46;
            {var subQ0=sQuery(id+"F0.wireOp",EDGE,"E12");Q46=makeQuery(id+"F0.imprint","IMPRINT",FACE,{"disambiguationData":[TD([[makeQuery(id+"F0.imprint","IMPRINT",EDGE,{"derivedFrom":subQ0}),-1.0]])]});}
            var Q47;
            {var subQ1=sQuery(id+"F0.wireOp",EDGE,"E257");Q47=makeQuery(id+"F0.imprint","IMPRINT",FACE,{"disambiguationData":[TD([[makeQuery(id+"F0.imprint","IMPRINT",EDGE,{"derivedFrom":subQ1}),1.0]])]});}
            var Q48;
            Q48=makeQuery(id+"F0.imprint","IMPRINT",FACE,{"disambiguationData":[TD([[makeQuery(id+"F0.imprint","IMPRINT",EDGE,{"derivedFrom":sQuery(id+"F0.wireOp",EDGE,"E242.bottom")}),-1.0]])]});
            var Q49;
            Q49=makeQuery(id+"F0.imprint","IMPRINT",FACE,{"disambiguationData":[TD([[makeQuery(id+"F0.imprint","IMPRINT",EDGE,{"derivedFrom":sQuery(id+"F0.wireOp",EDGE,"E139.bottom")}),-1.0]])]});
            var Q50;
            {var subQ0=sQuery(id+"F0.wireOp",EDGE,"E285");Q50=makeQuery(id+"F0.imprint","IMPRINT",FACE,{"disambiguationData":[TD([[makeQuery(id+"F0.imprint","IMPRINT",EDGE,{"derivedFrom":subQ0}),-1.0]])]});}
            var Q51;
            {var subQ3=sQuery(id+"F0.wireOp",EDGE,"E69");Q51=makeQuery(id+"F0.imprint","IMPRINT",FACE,{"disambiguationData":[TD([[makeQuery(id+"F0.imprint","IMPRINT",EDGE,{"derivedFrom":subQ3}),-1.0]])]});}
            var Q52;
            {var subQ7=sQuery(id+"F0.wireOp",EDGE,"E44");Q52=makeQuery(id+"F0.imprint","IMPRINT",FACE,{"disambiguationData":[TD([[makeQuery(id+"F0.imprint","IMPRINT",EDGE,{"derivedFrom":subQ7}),1.0]])]});}
            var Q53;
            {var subQ5=sQuery(id+"F0.wireOp",EDGE,"E259");Q53=makeQuery(id+"F0.imprint","IMPRINT",FACE,{"disambiguationData":[TD([[makeQuery(id+"F0.imprint","IMPRINT",EDGE,{"derivedFrom":subQ5}),-1.0]])]});}
            var Q54;
            {var subQ0=sQuery(id+"F0.wireOp",EDGE,"E241");var subQ3=sQuery(id+"F0.wireOp",EDGE,"E240");var subQ5=makeQuery(id+"F0.imprint","INTERSECT",VERTEX,{"derivedFrom":[subQ3,subQ0]});Q54=makeQuery(id+"F0.imprint","IMPRINT",FACE,{"disambiguationData":[TD([[makeQuery(id+"F0.imprint","IMPRINT",EDGE,{"disambiguationData":[TD([[subQ5,-1.0]])],"derivedFrom":subQ3}),1.0]])]});}
            var Q55;
            {var subQ54=sQuery(id+"F0.wireOp",EDGE,"E27");Q55=makeQuery(id+"F0.imprint","IMPRINT",FACE,{"disambiguationData":[TD([[makeQuery(id+"F0.imprint","IMPRINT",EDGE,{"derivedFrom":subQ54}),-1.0]])]});}
            var Q56;
            {var subQ4=sQuery(id+"F0.wireOp",EDGE,"E48");Q56=makeQuery(id+"F0.imprint","IMPRINT",FACE,{"disambiguationData":[TD([[makeQuery(id+"F0.imprint","IMPRINT",EDGE,{"derivedFrom":subQ4}),1.0]])]});}
            var Q57;
            {var subQ0=sQuery(id+"F0.wireOp",EDGE,"E237");Q57=makeQuery(id+"F0.imprint","IMPRINT",FACE,{"disambiguationData":[TD([[makeQuery(id+"F0.imprint","IMPRINT",EDGE,{"derivedFrom":subQ0}),1.0]])]});}
            var Q58;
            {var subQ1=sQuery(id+"F0.wireOp",EDGE,"E36");Q58=makeQuery(id+"F0.imprint","IMPRINT",FACE,{"disambiguationData":[TD([[makeQuery(id+"F0.imprint","IMPRINT",EDGE,{"derivedFrom":subQ1}),-1.0]])]});}
            var Q59;
            {var subQ2=sQuery(id+"F0.wireOp",EDGE,"E160");var subQ4=sQuery(id+"F0.wireOp",EDGE,"E153");var subQ5=makeQuery(id+"F0.imprint","INTERSECT",VERTEX,{"derivedFrom":[subQ4,subQ2]});Q59=makeQuery(id+"F0.imprint","IMPRINT",FACE,{"disambiguationData":[TD([[makeQuery(id+"F0.imprint","IMPRINT",EDGE,{"disambiguationData":[TD([[subQ5,-1.0]])],"derivedFrom":subQ4}),-1.0]])]});}
            var Q60;
            {var subQ1=sQuery(id+"F0.wireOp",EDGE,"E262");Q60=makeQuery(id+"F0.imprint","IMPRINT",FACE,{"disambiguationData":[TD([[makeQuery(id+"F0.imprint","IMPRINT",EDGE,{"derivedFrom":subQ1}),1.0]])]});}
            var Q61;
            {var subQ0=sQuery(id+"F0.wireOp",EDGE,"E69");Q61=makeQuery(id+"F0.imprint","IMPRINT",FACE,{"disambiguationData":[TD([[makeQuery(id+"F0.imprint","IMPRINT",EDGE,{"derivedFrom":subQ0}),1.0]])]});}
            var Q62;
            {var subQ0=sQuery(id+"F0.wireOp",EDGE,"E167");Q62=makeQuery(id+"F0.imprint","IMPRINT",FACE,{"disambiguationData":[TD([[makeQuery(id+"F0.imprint","IMPRINT",EDGE,{"derivedFrom":subQ0}),1.0]])]});}
            var Q63;
            {var subQ14=sQuery(id+"F0.wireOp",EDGE,"E12");Q63=makeQuery(id+"F0.imprint","IMPRINT",FACE,{"disambiguationData":[TD([[makeQuery(id+"F0.imprint","IMPRINT",EDGE,{"derivedFrom":subQ14}),1.0]])]});}
            var Q64;
            {var subQ5=sQuery(id+"F0.wireOp",EDGE,"E180");Q64=makeQuery(id+"F0.imprint","IMPRINT",FACE,{"disambiguationData":[TD([[makeQuery(id+"F0.imprint","IMPRINT",EDGE,{"derivedFrom":subQ5}),1.0]])]});}
            var Q65;
            {var subQ5=sQuery(id+"F0.wireOp",EDGE,"E204");Q65=makeQuery(id+"F0.imprint","IMPRINT",FACE,{"disambiguationData":[TD([[makeQuery(id+"F0.imprint","IMPRINT",EDGE,{"derivedFrom":subQ5}),-1.0]])]});}
            var Q66;
            {var subQ16=sQuery(id+"F0.wireOp",EDGE,"E141");Q66=makeQuery(id+"F0.imprint","IMPRINT",FACE,{"disambiguationData":[TD([[makeQuery(id+"F0.imprint","IMPRINT",EDGE,{"derivedFrom":subQ16}),1.0]])]});}
            var Q67;
            {var subQ5=sQuery(id+"F0.wireOp",EDGE,"E183");Q67=makeQuery(id+"F0.imprint","IMPRINT",FACE,{"disambiguationData":[TD([[makeQuery(id+"F0.imprint","IMPRINT",EDGE,{"derivedFrom":subQ5}),-1.0]])]});}
            var Q68;
            {var subQ5=sQuery(id+"F0.wireOp",EDGE,"E201");Q68=makeQuery(id+"F0.imprint","IMPRINT",FACE,{"disambiguationData":[TD([[makeQuery(id+"F0.imprint","IMPRINT",EDGE,{"derivedFrom":subQ5}),-1.0]])]});}
            var Q69;
            {var subQ5=sQuery(id+"F0.wireOp",EDGE,"E180");Q69=makeQuery(id+"F0.imprint","IMPRINT",FACE,{"disambiguationData":[TD([[makeQuery(id+"F0.imprint","IMPRINT",EDGE,{"derivedFrom":subQ5}),-1.0]])]});}
            var Q70;
            {var subQ5=sQuery(id+"F0.wireOp",EDGE,"E104");Q70=makeQuery(id+"F0.imprint","IMPRINT",FACE,{"disambiguationData":[TD([[makeQuery(id+"F0.imprint","IMPRINT",EDGE,{"derivedFrom":subQ5}),1.0]])]});}
            var Q71;
            {var subQ5=sQuery(id+"F0.wireOp",EDGE,"E247");Q71=makeQuery(id+"F0.imprint","IMPRINT",FACE,{"disambiguationData":[TD([[makeQuery(id+"F0.imprint","IMPRINT",EDGE,{"derivedFrom":subQ5}),1.0]])]});}
            var Q72;
            {var subQ1=sQuery(id+"F0.wireOp",EDGE,"E140");Q72=makeQuery(id+"F0.imprint","IMPRINT",FACE,{"disambiguationData":[TD([[makeQuery(id+"F0.imprint","IMPRINT",EDGE,{"derivedFrom":subQ1}),1.0]])]});}
            var Q73;
            {var subQ10=sQuery(id+"F0.wireOp",EDGE,"E239");Q73=makeQuery(id+"F0.imprint","IMPRINT",FACE,{"disambiguationData":[TD([[makeQuery(id+"F0.imprint","IMPRINT",EDGE,{"derivedFrom":subQ10}),-1.0]])]});}
            var Q74;
            {var subQ5=sQuery(id+"F0.wireOp",EDGE,"E186");Q74=makeQuery(id+"F0.imprint","IMPRINT",FACE,{"disambiguationData":[TD([[makeQuery(id+"F0.imprint","IMPRINT",EDGE,{"derivedFrom":subQ5}),-1.0]])]});}
            var Q75;
            {var subQ5=sQuery(id+"F0.wireOp",EDGE,"E201");Q75=makeQuery(id+"F0.imprint","IMPRINT",FACE,{"disambiguationData":[TD([[makeQuery(id+"F0.imprint","IMPRINT",EDGE,{"derivedFrom":subQ5}),1.0]])]});}
            var Q76;
            {var subQ6=sQuery(id+"F0.wireOp",EDGE,"E102");Q76=makeQuery(id+"F0.imprint","IMPRINT",FACE,{"disambiguationData":[TD([[makeQuery(id+"F0.imprint","IMPRINT",EDGE,{"derivedFrom":subQ6}),-1.0]])]});}
            var Q77;
            {var subQ4=sQuery(id+"F0.wireOp",EDGE,"E31.right");var subQ6=makeQuery(id+"F0.imprint","INTERSECT",VERTEX,{"derivedFrom":[subQ4,sQuery(id+"F0.wireOp",EDGE,"E74")]});Q77=makeQuery(id+"F0.imprint","IMPRINT",FACE,{"disambiguationData":[TD([[makeQuery(id+"F0.imprint","IMPRINT",EDGE,{"disambiguationData":[TD([[subQ6,-1.0]])],"derivedFrom":subQ4}),-1.0]])]});}
            var Q78;
            {var subQ5=sQuery(id+"F0.wireOp",EDGE,"E257");Q78=makeQuery(id+"F0.imprint","IMPRINT",FACE,{"disambiguationData":[TD([[makeQuery(id+"F0.imprint","IMPRINT",EDGE,{"derivedFrom":subQ5}),-1.0]])]});}
            var Q79;
            {var subQ5=sQuery(id+"F0.wireOp",EDGE,"E278");Q79=makeQuery(id+"F0.imprint","IMPRINT",FACE,{"disambiguationData":[TD([[makeQuery(id+"F0.imprint","IMPRINT",EDGE,{"derivedFrom":subQ5}),-1.0]])]});}
            var Q80;
            {var subQ13=sQuery(id+"F0.wireOp",EDGE,"E254");var subQ16=sQuery(id+"F0.wireOp",EDGE,"E219");var subQ17=makeQuery(id+"F0.imprint","INTERSECT",VERTEX,{"derivedFrom":[subQ16,subQ13]});Q80=makeQuery(id+"F0.imprint","IMPRINT",FACE,{"disambiguationData":[TD([[makeQuery(id+"F0.imprint","IMPRINT",EDGE,{"disambiguationData":[TD([[subQ17,-1.0]])],"derivedFrom":subQ16}),-1.0]])]});}
            var Q81;
            {var subQ5=sQuery(id+"F0.wireOp",EDGE,"E183");Q81=makeQuery(id+"F0.imprint","IMPRINT",FACE,{"disambiguationData":[TD([[makeQuery(id+"F0.imprint","IMPRINT",EDGE,{"derivedFrom":subQ5}),1.0]])]});}
            var Q82;
            {var subQ5=sQuery(id+"F0.wireOp",EDGE,"E204");Q82=makeQuery(id+"F0.imprint","IMPRINT",FACE,{"disambiguationData":[TD([[makeQuery(id+"F0.imprint","IMPRINT",EDGE,{"derivedFrom":subQ5}),1.0]])]});}
            var Q83;
            {var subQ0=sQuery(id+"F0.wireOp",EDGE,"E147");Q83=makeQuery(id+"F0.imprint","IMPRINT",FACE,{"disambiguationData":[TD([[makeQuery(id+"F0.imprint","IMPRINT",EDGE,{"derivedFrom":subQ0}),-1.0]])]});}
            var Q84;
            {var subQ0=sQuery(id+"F0.wireOp",EDGE,"E120");var subQ11=sQuery(id+"F0.wireOp",EDGE,"E89");var subQ16=makeQuery(id+"F0.imprint","INTERSECT",VERTEX,{"derivedFrom":[subQ11,subQ0]});Q84=makeQuery(id+"F0.imprint","IMPRINT",FACE,{"disambiguationData":[TD([[makeQuery(id+"F0.imprint","IMPRINT",EDGE,{"disambiguationData":[TD([[subQ16,1.0]])],"derivedFrom":subQ11}),1.0]])]});}
            var Q85;
            {var subQ0=sQuery(id+"F0.wireOp",EDGE,"E212");Q85=makeQuery(id+"F0.imprint","IMPRINT",FACE,{"disambiguationData":[TD([[makeQuery(id+"F0.imprint","IMPRINT",EDGE,{"derivedFrom":subQ0}),1.0]])]});}
            var Q86;
            {var subQ5=sQuery(id+"F0.wireOp",EDGE,"E198");Q86=makeQuery(id+"F0.imprint","IMPRINT",FACE,{"disambiguationData":[TD([[makeQuery(id+"F0.imprint","IMPRINT",EDGE,{"derivedFrom":subQ5}),-1.0]])]});}
            var Q87;
            {var subQ8=sQuery(id+"F0.wireOp",EDGE,"E105");Q87=makeQuery(id+"F0.imprint","IMPRINT",FACE,{"disambiguationData":[TD([[makeQuery(id+"F0.imprint","IMPRINT",EDGE,{"derivedFrom":subQ8}),1.0]])]});}
            var Q88;
            {var subQ5=sQuery(id+"F0.wireOp",EDGE,"E270");Q88=makeQuery(id+"F0.imprint","IMPRINT",FACE,{"disambiguationData":[TD([[makeQuery(id+"F0.imprint","IMPRINT",EDGE,{"derivedFrom":subQ5}),1.0]])]});}
            var Q89;
            {var subQ0=sQuery(id+"F0.wireOp",EDGE,"E118.trimOffspring");Q89=makeQuery(id+"F0.imprint","IMPRINT",FACE,{"disambiguationData":[TD([[makeQuery(id+"F0.imprint","IMPRINT",EDGE,{"derivedFrom":subQ0}),-1.0]])]});}
            var Q90;
            {var subQ5=sQuery(id+"F0.wireOp",EDGE,"E131");Q90=makeQuery(id+"F0.imprint","IMPRINT",FACE,{"disambiguationData":[TD([[makeQuery(id+"F0.imprint","IMPRINT",EDGE,{"derivedFrom":subQ5}),-1.0]])]});}
            var Q91;
            {var subQ5=sQuery(id+"F0.wireOp",EDGE,"E189");Q91=makeQuery(id+"F0.imprint","IMPRINT",FACE,{"disambiguationData":[TD([[makeQuery(id+"F0.imprint","IMPRINT",EDGE,{"derivedFrom":subQ5}),-1.0]])]});}
            var Q92;
            {var subQ2=sQuery(id+"F0.wireOp",EDGE,"E31.left");var subQ5=sQuery(id+"F0.wireOp",EDGE,"E114");var subQ7=makeQuery(id+"F0.imprint","INTERSECT",VERTEX,{"derivedFrom":[subQ2,subQ5]});Q92=makeQuery(id+"F0.imprint","IMPRINT",FACE,{"disambiguationData":[TD([[makeQuery(id+"F0.imprint","IMPRINT",EDGE,{"disambiguationData":[TD([[subQ7,1.0]])],"derivedFrom":subQ2}),1.0]])]});}
            var Q93;
            {var subQ0=sQuery(id+"F0.wireOp",EDGE,"E206");var subQ5=sQuery(id+"F0.wireOp",EDGE,"E23");var subQ6=makeQuery(id+"F0.imprint","INTERSECT",VERTEX,{"derivedFrom":[subQ5,subQ0]});Q93=makeQuery(id+"F0.imprint","IMPRINT",FACE,{"disambiguationData":[TD([[makeQuery(id+"F0.imprint","IMPRINT",EDGE,{"disambiguationData":[TD([[subQ6,1.0]])],"derivedFrom":subQ5}),1.0]])]});}
            var Q94;
            {var subQ5=sQuery(id+"F0.wireOp",EDGE,"E192");Q94=makeQuery(id+"F0.imprint","IMPRINT",FACE,{"disambiguationData":[TD([[makeQuery(id+"F0.imprint","IMPRINT",EDGE,{"derivedFrom":subQ5}),-1.0]])]});}
            var Q95;
            {var subQ0=sQuery(id+"F0.wireOp",EDGE,"E165");Q95=makeQuery(id+"F0.imprint","IMPRINT",FACE,{"disambiguationData":[TD([[makeQuery(id+"F0.imprint","IMPRINT",EDGE,{"derivedFrom":subQ0}),-1.0]])]});}
            var Q96;
            {var subQ1=sQuery(id+"F0.wireOp",EDGE,"E21");Q96=makeQuery(id+"F0.imprint","IMPRINT",FACE,{"disambiguationData":[TD([[makeQuery(id+"F0.imprint","IMPRINT",EDGE,{"derivedFrom":subQ1}),1.0]])]});}
            var Q97;
            {var subQ0=sQuery(id+"F0.wireOp",EDGE,"E210");Q97=makeQuery(id+"F0.imprint","IMPRINT",FACE,{"disambiguationData":[TD([[makeQuery(id+"F0.imprint","IMPRINT",EDGE,{"derivedFrom":subQ0}),-1.0]])]});}
            var Q98;
            {var subQ5=sQuery(id+"F0.wireOp",EDGE,"E197");Q98=makeQuery(id+"F0.imprint","IMPRINT",FACE,{"disambiguationData":[TD([[makeQuery(id+"F0.imprint","IMPRINT",EDGE,{"derivedFrom":subQ5}),1.0]])]});}
            var Q99;
            {var subQ8=sQuery(id+"F0.wireOp",EDGE,"E112");Q99=makeQuery(id+"F0.imprint","IMPRINT",FACE,{"disambiguationData":[TD([[makeQuery(id+"F0.imprint","IMPRINT",EDGE,{"derivedFrom":subQ8}),-1.0]])]});}
            var Q100;
            {var subQ0=sQuery(id+"F0.wireOp",EDGE,"E263");var subQ3=sQuery(id+"F0.wireOp",EDGE,"E115");var subQ4=makeQuery(id+"F0.imprint","INTERSECT",VERTEX,{"derivedFrom":[subQ3,subQ0]});Q100=makeQuery(id+"F0.imprint","IMPRINT",FACE,{"disambiguationData":[TD([[makeQuery(id+"F0.imprint","IMPRINT",EDGE,{"disambiguationData":[TD([[subQ4,-1.0]])],"derivedFrom":subQ3}),-1.0]])]});}
            var Q101;
            {var subQ1=sQuery(id+"F0.wireOp",EDGE,"E59");var subQ6=sQuery(id+"F0.wireOp",EDGE,"E190");var subQ9=makeQuery(id+"F0.imprint","INTERSECT",VERTEX,{"derivedFrom":[subQ1,subQ6]});Q101=makeQuery(id+"F0.imprint","IMPRINT",FACE,{"disambiguationData":[TD([[makeQuery(id+"F0.imprint","IMPRINT",EDGE,{"disambiguationData":[TD([[subQ9,1.0]])],"derivedFrom":subQ1}),1.0]])]});}
            var Q102;
            {var subQ5=sQuery(id+"F0.wireOp",EDGE,"E177");Q102=makeQuery(id+"F0.imprint","IMPRINT",FACE,{"disambiguationData":[TD([[makeQuery(id+"F0.imprint","IMPRINT",EDGE,{"derivedFrom":subQ5}),-1.0]])]});}
            var Q103;
            {var subQ5=sQuery(id+"F0.wireOp",EDGE,"E147");Q103=makeQuery(id+"F0.imprint","IMPRINT",FACE,{"disambiguationData":[TD([[makeQuery(id+"F0.imprint","IMPRINT",EDGE,{"derivedFrom":subQ5}),1.0]])]});}
            var Q104;
            {var subQ8=sQuery(id+"F0.wireOp",EDGE,"E237");Q104=makeQuery(id+"F0.imprint","IMPRINT",FACE,{"disambiguationData":[TD([[makeQuery(id+"F0.imprint","IMPRINT",EDGE,{"derivedFrom":subQ8}),-1.0]])]});}
            var Q105;
            {var subQ5=sQuery(id+"F0.wireOp",EDGE,"E206");var subQ9=sQuery(id+"F0.wireOp",EDGE,"E23");var subQ11=makeQuery(id+"F0.imprint","INTERSECT",VERTEX,{"derivedFrom":[subQ9,subQ5]});Q105=makeQuery(id+"F0.imprint","IMPRINT",FACE,{"disambiguationData":[TD([[makeQuery(id+"F0.imprint","IMPRINT",EDGE,{"disambiguationData":[TD([[subQ11,-1.0]])],"derivedFrom":subQ9}),1.0]])]});}
            var Q106;
            {var subQ5=sQuery(id+"F0.wireOp",EDGE,"E189");Q106=makeQuery(id+"F0.imprint","IMPRINT",FACE,{"disambiguationData":[TD([[makeQuery(id+"F0.imprint","IMPRINT",EDGE,{"derivedFrom":subQ5}),1.0]])]});}
            var Q107;
            {var subQ3=sQuery(id+"F0.wireOp",EDGE,"E23");var subQ8=sQuery(id+"F0.wireOp",EDGE,"E206");var subQ11=makeQuery(id+"F0.imprint","INTERSECT",VERTEX,{"derivedFrom":[subQ3,subQ8]});Q107=makeQuery(id+"F0.imprint","IMPRINT",FACE,{"disambiguationData":[TD([[makeQuery(id+"F0.imprint","IMPRINT",EDGE,{"disambiguationData":[TD([[subQ11,1.0]])],"derivedFrom":subQ3}),-1.0]])]});}
            var Q108;
            {var subQ7=sQuery(id+"F0.wireOp",EDGE,"E101");Q108=makeQuery(id+"F0.imprint","IMPRINT",FACE,{"disambiguationData":[TD([[makeQuery(id+"F0.imprint","IMPRINT",EDGE,{"derivedFrom":subQ7}),-1.0]])]});}
            var Q109;
            {var subQ3=sQuery(id+"F0.wireOp",EDGE,"E111");Q109=makeQuery(id+"F0.imprint","IMPRINT",FACE,{"disambiguationData":[TD([[makeQuery(id+"F0.imprint","IMPRINT",EDGE,{"derivedFrom":subQ3}),1.0]])]});}
            var Q110;
            {var subQ2=sQuery(id+"F0.wireOp",EDGE,"E150");Q110=makeQuery(id+"F0.imprint","IMPRINT",FACE,{"disambiguationData":[TD([[makeQuery(id+"F0.imprint","IMPRINT",EDGE,{"derivedFrom":subQ2}),-1.0]])]});}
            var Q111;
            {var subQ1=sQuery(id+"F0.wireOp",EDGE,"E92");var subQ3=sQuery(id+"F0.wireOp",EDGE,"E31.right");var subQ4=makeQuery(id+"F0.imprint","INTERSECT",VERTEX,{"derivedFrom":[subQ3,subQ1]});Q111=makeQuery(id+"F0.imprint","IMPRINT",FACE,{"disambiguationData":[TD([[makeQuery(id+"F0.imprint","IMPRINT",EDGE,{"disambiguationData":[TD([[subQ4,1.0]])],"derivedFrom":subQ3}),-1.0]])]});}
            var Q112;
            {var subQ5=sQuery(id+"F0.wireOp",EDGE,"E256");Q112=makeQuery(id+"F0.imprint","IMPRINT",FACE,{"disambiguationData":[TD([[makeQuery(id+"F0.imprint","IMPRINT",EDGE,{"derivedFrom":subQ5}),1.0]])]});}
            var Q113;
            {var subQ5=sQuery(id+"F0.wireOp",EDGE,"E218");Q113=makeQuery(id+"F0.imprint","IMPRINT",FACE,{"disambiguationData":[TD([[makeQuery(id+"F0.imprint","IMPRINT",EDGE,{"derivedFrom":subQ5}),-1.0]])]});}
            var Q114;
            {var subQ4=sQuery(id+"F0.wireOp",EDGE,"E109");Q114=makeQuery(id+"F0.imprint","IMPRINT",FACE,{"disambiguationData":[TD([[makeQuery(id+"F0.imprint","IMPRINT",EDGE,{"derivedFrom":subQ4}),1.0]])]});}
            var Q115;
            {var subQ5=sQuery(id+"F0.wireOp",EDGE,"E192");Q115=makeQuery(id+"F0.imprint","IMPRINT",FACE,{"disambiguationData":[TD([[makeQuery(id+"F0.imprint","IMPRINT",EDGE,{"derivedFrom":subQ5}),1.0]])]});}
            var Q116;
            Q116=makeQuery(id+"F0.imprint","IMPRINT",FACE,{"disambiguationData":[TD([[makeQuery(id+"F0.imprint","IMPRINT",EDGE,{"derivedFrom":sQuery(id+"F0.wireOp",EDGE,"E132")}),1.0]])]});
            var Q117;
            Q117=makeQuery(id+"F0.imprint","IMPRINT",FACE,{"disambiguationData":[TD([[makeQuery(id+"F0.imprint","IMPRINT",EDGE,{"derivedFrom":sQuery(id+"F0.wireOp",EDGE,"E148")}),1.0]])]});
            var Q118;
            Q118=makeQuery(id+"F0.imprint","IMPRINT",FACE,{"disambiguationData":[TD([[makeQuery(id+"F0.imprint","IMPRINT",EDGE,{"derivedFrom":sQuery(id+"F0.wireOp",EDGE,"E228")}),1.0]])]});
            var Q119;
            {var subQ6=sQuery(id+"F0.wireOp",EDGE,"E115");var subQ7=sQuery(id+"F0.wireOp",EDGE,"E67");var subQ8=makeQuery(id+"F0.imprint","INTERSECT",VERTEX,{"derivedFrom":[subQ7,subQ6]});Q119=makeQuery(id+"F0.imprint","IMPRINT",FACE,{"disambiguationData":[TD([[makeQuery(id+"F0.imprint","IMPRINT",EDGE,{"disambiguationData":[TD([[subQ8,1.0]])],"derivedFrom":subQ7}),1.0]])]});}
            var Q120;
            {var subQ0=sQuery(id+"F0.wireOp",EDGE,"E274");Q120=makeQuery(id+"F0.imprint","IMPRINT",FACE,{"disambiguationData":[TD([[makeQuery(id+"F0.imprint","IMPRINT",EDGE,{"derivedFrom":subQ0}),1.0]])]});}
            var Q121;
            {var subQ5=sQuery(id+"F0.wireOp",EDGE,"E209");Q121=makeQuery(id+"F0.imprint","IMPRINT",FACE,{"disambiguationData":[TD([[makeQuery(id+"F0.imprint","IMPRINT",EDGE,{"derivedFrom":subQ5}),-1.0]])]});}
            var Q122;
            {var subQ1=sQuery(id+"F0.wireOp",EDGE,"E260");Q122=makeQuery(id+"F0.imprint","IMPRINT",FACE,{"disambiguationData":[TD([[makeQuery(id+"F0.imprint","IMPRINT",EDGE,{"derivedFrom":subQ1}),1.0]])]});}
            var Q123;
            {var subQ0=sQuery(id+"F0.wireOp",EDGE,"E236");Q123=makeQuery(id+"F0.imprint","IMPRINT",FACE,{"disambiguationData":[TD([[makeQuery(id+"F0.imprint","IMPRINT",EDGE,{"derivedFrom":subQ0}),-1.0]])]});}
            var Q124;
            {var subQ4=sQuery(id+"F0.wireOp",EDGE,"E159");Q124=makeQuery(id+"F0.imprint","IMPRINT",FACE,{"disambiguationData":[TD([[makeQuery(id+"F0.imprint","IMPRINT",EDGE,{"derivedFrom":subQ4}),1.0]])]});}
            var Q125;
            {var subQ5=sQuery(id+"F0.wireOp",EDGE,"E209");Q125=makeQuery(id+"F0.imprint","IMPRINT",FACE,{"disambiguationData":[TD([[makeQuery(id+"F0.imprint","IMPRINT",EDGE,{"derivedFrom":subQ5}),1.0]])]});}
            var Q126;
            {var subQ5=sQuery(id+"F0.wireOp",EDGE,"E186");Q126=makeQuery(id+"F0.imprint","IMPRINT",FACE,{"disambiguationData":[TD([[makeQuery(id+"F0.imprint","IMPRINT",EDGE,{"derivedFrom":subQ5}),1.0]])]});}
            var Q127;
            {var subQ5=sQuery(id+"F0.wireOp",EDGE,"E197");Q127=makeQuery(id+"F0.imprint","IMPRINT",FACE,{"disambiguationData":[TD([[makeQuery(id+"F0.imprint","IMPRINT",EDGE,{"derivedFrom":subQ5}),-1.0]])]});}
            var Q128;
            {var subQ8=sQuery(id+"F0.wireOp",EDGE,"E67");var subQ11=sQuery(id+"F0.wireOp",EDGE,"E99");var subQ13=makeQuery(id+"F0.imprint","INTERSECT",VERTEX,{"derivedFrom":[subQ8,subQ11]});Q128=makeQuery(id+"F0.imprint","IMPRINT",FACE,{"disambiguationData":[TD([[makeQuery(id+"F0.imprint","IMPRINT",EDGE,{"disambiguationData":[TD([[subQ13,-1.0]])],"derivedFrom":subQ8}),1.0]])]});}
            var Q129;
            {var subQ4=sQuery(id+"F0.wireOp",EDGE,"E56");var subQ6=sQuery(id+"F0.wireOp",EDGE,"E195");var subQ8=makeQuery(id+"F0.imprint","INTERSECT",VERTEX,{"derivedFrom":[subQ4,subQ6]});Q129=makeQuery(id+"F0.imprint","IMPRINT",FACE,{"disambiguationData":[TD([[makeQuery(id+"F0.imprint","IMPRINT",EDGE,{"disambiguationData":[TD([[subQ8,1.0]])],"derivedFrom":subQ4}),1.0]])]});}
            var Q130;
            {var subQ10=sQuery(id+"F0.wireOp",EDGE,"E110");Q130=makeQuery(id+"F0.imprint","IMPRINT",FACE,{"disambiguationData":[TD([[makeQuery(id+"F0.imprint","IMPRINT",EDGE,{"derivedFrom":subQ10}),1.0]])]});}
            var Q131;
            {var subQ5=sQuery(id+"F0.wireOp",EDGE,"E144");Q131=makeQuery(id+"F0.imprint","IMPRINT",FACE,{"disambiguationData":[TD([[makeQuery(id+"F0.imprint","IMPRINT",EDGE,{"derivedFrom":subQ5}),-1.0]])]});}
            var Q132;
            {var subQ5=sQuery(id+"F0.wireOp",EDGE,"E157");Q132=makeQuery(id+"F0.imprint","IMPRINT",FACE,{"disambiguationData":[TD([[makeQuery(id+"F0.imprint","IMPRINT",EDGE,{"derivedFrom":subQ5}),-1.0]])]});}
            var Q133;
            {var subQ5=sQuery(id+"F0.wireOp",EDGE,"E270");Q133=makeQuery(id+"F0.imprint","IMPRINT",FACE,{"disambiguationData":[TD([[makeQuery(id+"F0.imprint","IMPRINT",EDGE,{"derivedFrom":subQ5}),-1.0]])]});}
            var Q134;
            {var subQ1=sQuery(id+"F0.wireOp",EDGE,"E174");var subQ4=sQuery(id+"F0.wireOp",EDGE,"E68");var subQ5=makeQuery(id+"F0.imprint","INTERSECT",VERTEX,{"derivedFrom":[subQ4,subQ1]});Q134=makeQuery(id+"F0.imprint","IMPRINT",FACE,{"disambiguationData":[TD([[makeQuery(id+"F0.imprint","IMPRINT",EDGE,{"disambiguationData":[TD([[subQ5,1.0]])],"derivedFrom":subQ4}),1.0]])]});}
            var Q135;
            {var subQ5=sQuery(id+"F0.wireOp",EDGE,"E157");Q135=makeQuery(id+"F0.imprint","IMPRINT",FACE,{"disambiguationData":[TD([[makeQuery(id+"F0.imprint","IMPRINT",EDGE,{"derivedFrom":subQ5}),1.0]])]});}
            var Q136;
            {var subQ5=sQuery(id+"F0.wireOp",EDGE,"E247");Q136=makeQuery(id+"F0.imprint","IMPRINT",FACE,{"disambiguationData":[TD([[makeQuery(id+"F0.imprint","IMPRINT",EDGE,{"derivedFrom":subQ5}),-1.0]])]});}
            var Q137;
            {var subQ5=sQuery(id+"F0.wireOp",EDGE,"E131");Q137=makeQuery(id+"F0.imprint","IMPRINT",FACE,{"disambiguationData":[TD([[makeQuery(id+"F0.imprint","IMPRINT",EDGE,{"derivedFrom":subQ5}),1.0]])]});}
            var Q138;
            {var subQ5=sQuery(id+"F0.wireOp",EDGE,"E172");Q138=makeQuery(id+"F0.imprint","IMPRINT",FACE,{"disambiguationData":[TD([[makeQuery(id+"F0.imprint","IMPRINT",EDGE,{"derivedFrom":subQ5}),1.0]])]});}
            var Q139;
            {var subQ0=sQuery(id+"F0.wireOp",EDGE,"E244");var subQ1=sQuery(id+"F0.wireOp",EDGE,"E234");var subQ2=makeQuery(id+"F0.imprint","INTERSECT",VERTEX,{"derivedFrom":[subQ1,subQ0]});Q139=makeQuery(id+"F0.imprint","IMPRINT",FACE,{"disambiguationData":[TD([[makeQuery(id+"F0.imprint","IMPRINT",EDGE,{"disambiguationData":[TD([[subQ2,1.0]])],"derivedFrom":subQ1}),-1.0]])]});}
            var Q140;
            {var subQ5=sQuery(id+"F0.wireOp",EDGE,"E172");Q140=makeQuery(id+"F0.imprint","IMPRINT",FACE,{"disambiguationData":[TD([[makeQuery(id+"F0.imprint","IMPRINT",EDGE,{"derivedFrom":subQ5}),-1.0]])]});}
            var Q141;
            {var subQ5=sQuery(id+"F0.wireOp",EDGE,"E137");Q141=makeQuery(id+"F0.imprint","IMPRINT",FACE,{"disambiguationData":[TD([[makeQuery(id+"F0.imprint","IMPRINT",EDGE,{"derivedFrom":subQ5}),1.0]])]});}
            var Q142;
            {var subQ5=sQuery(id+"F0.wireOp",EDGE,"E177");Q142=makeQuery(id+"F0.imprint","IMPRINT",FACE,{"disambiguationData":[TD([[makeQuery(id+"F0.imprint","IMPRINT",EDGE,{"derivedFrom":subQ5}),1.0]])]});}
            var Q143;
            {var subQ0=sQuery(id+"F0.wireOp",EDGE,"E123");Q143=makeQuery(id+"F0.imprint","IMPRINT",FACE,{"disambiguationData":[TD([[makeQuery(id+"F0.imprint","IMPRINT",EDGE,{"derivedFrom":subQ0}),-1.0]])]});}
            var Q144;
            {var subQ5=sQuery(id+"F0.wireOp",EDGE,"E198");Q144=makeQuery(id+"F0.imprint","IMPRINT",FACE,{"disambiguationData":[TD([[makeQuery(id+"F0.imprint","IMPRINT",EDGE,{"derivedFrom":subQ5}),1.0]])]});}
            var Q145;
            {var subQ5=sQuery(id+"F0.wireOp",EDGE,"E218");Q145=makeQuery(id+"F0.imprint","IMPRINT",FACE,{"disambiguationData":[TD([[makeQuery(id+"F0.imprint","IMPRINT",EDGE,{"derivedFrom":subQ5}),1.0]])]});}
            var Q146;
            {var subQ1=sQuery(id+"F0.wireOp",EDGE,"E244");var subQ5=sQuery(id+"F0.wireOp",EDGE,"E94");var subQ8=makeQuery(id+"F0.imprint","INTERSECT",VERTEX,{"derivedFrom":[subQ5,subQ1]});Q146=makeQuery(id+"F0.imprint","IMPRINT",FACE,{"disambiguationData":[TD([[makeQuery(id+"F0.imprint","IMPRINT",EDGE,{"disambiguationData":[TD([[subQ8,1.0]])],"derivedFrom":subQ5}),1.0]])]});}
            var Q147;
            {var subQ0=sQuery(id+"F0.wireOp",EDGE,"E230");Q147=makeQuery(id+"F0.imprint","IMPRINT",FACE,{"disambiguationData":[TD([[makeQuery(id+"F0.imprint","IMPRINT",EDGE,{"derivedFrom":subQ0}),-1.0]])]});}
            var Q148;
            {var subQ6=sQuery(id+"F0.wireOp",EDGE,"E158");Q148=makeQuery(id+"F0.imprint","IMPRINT",FACE,{"disambiguationData":[TD([[makeQuery(id+"F0.imprint","IMPRINT",EDGE,{"derivedFrom":subQ6}),1.0]])]});}
            var Q149;
            {var subQ4=sQuery(id+"F0.wireOp",EDGE,"E125.bottom");Q149=makeQuery(id+"F0.imprint","IMPRINT",FACE,{"disambiguationData":[TD([[makeQuery(id+"F0.imprint","IMPRINT",EDGE,{"derivedFrom":subQ4}),-1.0]])]});}
            var Q150;
            {var subQ0=sQuery(id+"F0.wireOp",EDGE,"E126");Q150=makeQuery(id+"F0.imprint","IMPRINT",FACE,{"disambiguationData":[TD([[makeQuery(id+"F0.imprint","IMPRINT",EDGE,{"derivedFrom":subQ0}),1.0]])]});}
            var Q151;
            Q151=makeQuery(id+"F0.imprint","IMPRINT",FACE,{"disambiguationData":[TD([[makeQuery(id+"F0.imprint","IMPRINT",EDGE,{"derivedFrom":sQuery(id+"F0.wireOp",EDGE,"E138.top")}),1.0]])]});
            var Q152;
            Q152=makeQuery(id+"F0.imprint","IMPRINT",FACE,{"disambiguationData":[TD([[makeQuery(id+"F0.imprint","IMPRINT",EDGE,{"derivedFrom":sQuery(id+"F0.wireOp",EDGE,"E229.top")}),1.0]])]});
            var Q153;
            {var subQ0=sQuery(id+"F0.wireOp",EDGE,"E224");Q153=makeQuery(id+"F0.imprint","IMPRINT",FACE,{"disambiguationData":[TD([[makeQuery(id+"F0.imprint","IMPRINT",EDGE,{"derivedFrom":subQ0}),-1.0]])]});}
            var Q154;
            {var subQ5=sQuery(id+"F0.wireOp",EDGE,"E256");Q154=makeQuery(id+"F0.imprint","IMPRINT",FACE,{"disambiguationData":[TD([[makeQuery(id+"F0.imprint","IMPRINT",EDGE,{"derivedFrom":subQ5}),-1.0]])]});}
            var Q155;
            {var subQ5=sQuery(id+"F0.wireOp",EDGE,"E267");Q155=makeQuery(id+"F0.imprint","IMPRINT",FACE,{"disambiguationData":[TD([[makeQuery(id+"F0.imprint","IMPRINT",EDGE,{"derivedFrom":subQ5}),-1.0]])]});}
            var Q156;
            {var subQ5=sQuery(id+"F0.wireOp",EDGE,"E273");Q156=makeQuery(id+"F0.imprint","IMPRINT",FACE,{"disambiguationData":[TD([[makeQuery(id+"F0.imprint","IMPRINT",EDGE,{"derivedFrom":subQ5}),1.0]])]});}
            var Q157;
            {var subQ5=sQuery(id+"F0.wireOp",EDGE,"E267");Q157=makeQuery(id+"F0.imprint","IMPRINT",FACE,{"disambiguationData":[TD([[makeQuery(id+"F0.imprint","IMPRINT",EDGE,{"derivedFrom":subQ5}),1.0]])]});}
            var Q158;
            {var subQ0=sQuery(id+"F0.wireOp",EDGE,"E219");var subQ8=makeQuery(id+"F0.imprint","INTERSECT",VERTEX,{"derivedFrom":[sQuery(id+"F0.wireOp",EDGE,"E173"),subQ0]});Q158=makeQuery(id+"F0.imprint","IMPRINT",FACE,{"disambiguationData":[TD([[makeQuery(id+"F0.imprint","IMPRINT",EDGE,{"disambiguationData":[TD([[subQ8,-1.0]])],"derivedFrom":subQ0}),-1.0]])]});}
            var Q159;
            {var subQ5=sQuery(id+"F0.wireOp",EDGE,"E273");Q159=makeQuery(id+"F0.imprint","IMPRINT",FACE,{"disambiguationData":[TD([[makeQuery(id+"F0.imprint","IMPRINT",EDGE,{"derivedFrom":subQ5}),-1.0]])]});}
            var Q160;
            {var subQ5=sQuery(id+"F0.wireOp",EDGE,"E278");Q160=makeQuery(id+"F0.imprint","IMPRINT",FACE,{"disambiguationData":[TD([[makeQuery(id+"F0.imprint","IMPRINT",EDGE,{"derivedFrom":subQ5}),1.0]])]});}
            var Q161;
            {var subQ5=sQuery(id+"F0.wireOp",EDGE,"E250");Q161=makeQuery(id+"F0.imprint","IMPRINT",FACE,{"disambiguationData":[TD([[makeQuery(id+"F0.imprint","IMPRINT",EDGE,{"derivedFrom":subQ5}),-1.0]])]});}
            var Q162;
            {var subQ5=sQuery(id+"F0.wireOp",EDGE,"E144");Q162=makeQuery(id+"F0.imprint","IMPRINT",FACE,{"disambiguationData":[TD([[makeQuery(id+"F0.imprint","IMPRINT",EDGE,{"derivedFrom":subQ5}),1.0]])]});}
            var Q163;
            {var subQ5=sQuery(id+"F0.wireOp",EDGE,"E250");Q163=makeQuery(id+"F0.imprint","IMPRINT",FACE,{"disambiguationData":[TD([[makeQuery(id+"F0.imprint","IMPRINT",EDGE,{"derivedFrom":subQ5}),1.0]])]});}
            var Q164;
            {var subQ0=sQuery(id+"F0.wireOp",EDGE,"E176");var subQ1=sQuery(id+"F0.wireOp",EDGE,"E173");var subQ2=makeQuery(id+"F0.imprint","INTERSECT",VERTEX,{"derivedFrom":[subQ1,subQ0]});Q164=makeQuery(id+"F0.imprint","IMPRINT",FACE,{"disambiguationData":[TD([[makeQuery(id+"F0.imprint","IMPRINT",EDGE,{"disambiguationData":[TD([[subQ2,-1.0]])],"derivedFrom":subQ1}),-1.0]])]});}
            var Q165;
            {var subQ5=sQuery(id+"F0.wireOp",EDGE,"E137");Q165=makeQuery(id+"F0.imprint","IMPRINT",FACE,{"disambiguationData":[TD([[makeQuery(id+"F0.imprint","IMPRINT",EDGE,{"derivedFrom":subQ5}),-1.0]])]});}
            var Q166;
            {var subQ1=sQuery(id+"F0.wireOp",EDGE,"E31.left");var subQ8=makeQuery(id+"F0.imprint","INTERSECT",VERTEX,{"derivedFrom":[subQ1,sQuery(id+"F0.wireOp",EDGE,"E47")]});Q166=makeQuery(id+"F0.imprint","IMPRINT",FACE,{"disambiguationData":[TD([[makeQuery(id+"F0.imprint","IMPRINT",EDGE,{"disambiguationData":[TD([[subQ8,-1.0]])],"derivedFrom":subQ1}),1.0]])]});}
            extrude(context, id + "F1", {"entities" : qUnion([Q0, Q1, Q2, Q3, Q4, Q5, Q6, Q7, Q8, Q9, Q10, Q11, Q12, Q13, Q14, Q15, Q16, Q17, Q18, Q19, Q20, Q21, Q22, Q23, Q24, Q25, Q26, Q27, Q28, Q29, Q30, Q31, Q32, Q33, Q34, Q35, Q36, Q37, Q38, Q39, Q40, Q41, Q42, Q43, Q44, Q45, Q46, Q47, Q48, Q49, Q50, Q51, Q52, Q53, Q54, Q55, Q56, Q57, Q58, Q59, Q60, Q61, Q62, Q63, Q64, Q65, Q66, Q67, Q68, Q69, Q70, Q71, Q72, Q73, Q74, Q75, Q76, Q77, Q78, Q79, Q80, Q81, Q82, Q83, Q84, Q85, Q86, Q87, Q88, Q89, Q90, Q91, Q92, Q93, Q94, Q95, Q96, Q97, Q98, Q99, Q100, Q101, Q102, Q103, Q104, Q105, Q106, Q107, Q108, Q109, Q110, Q111, Q112, Q113, Q114, Q115, Q116, Q117, Q118, Q119, Q120, Q121, Q122, Q123, Q124, Q125, Q126, Q127, Q128, Q129, Q130, Q131, Q132, Q133, Q134, Q135, Q136, Q137, Q138, Q139, Q140, Q141, Q142, Q143, Q144, Q145, Q146, Q147, Q148, Q149, Q150, Q151, Q152, Q153, Q154, Q155, Q156, Q157, Q158, Q159, Q160, Q161, Q162, Q163, Q164, Q165, Q166]), "depth" : 8229.6 * mm, "offsetDistance" : 25.4 * mm});
        }
        {
            var Q0;
            Q0=makeQuery(id+"F1.opExtrude","SWEPT_FACE",FACE,{"disambiguationData":[OSD([sQuery(id+"F0.wireOp",EDGE,"E30")])]});
            var sketch = newSketch(context, id + "F2", { "sketchPlane" : qUnion([Q0])});
            skLineSegment(sketch, "E288", {"start": v(-304.8, 304.8) * mm, "end": v(7762.88, 5683.25) * mm});
            skLineSegment(sketch, "E289", {"start": v(7762.87, 5683.25) * mm, "end": v(15830.55, 304.8) * mm});
            skLineSegment(sketch, "E290", {"start": v(15830.55, 304.8) * mm, "end": v(15830.55, 0) * mm});
            skLineSegment(sketch, "E291", {"start": v(15830.55, 0) * mm, "end": v(-304.8, 0) * mm});
            skLineSegment(sketch, "E292", {"start": v(-304.8, 0) * mm, "end": v(-304.8, 304.8) * mm});
            skLineSegment(sketch, "E293", {"start": v(-304.8, 304.8) * mm, "end": v(0, 304.8) * mm, "construction": true});
            skLineSegment(sketch, "E294", {"start": v(0, 304.8) * mm, "end": v(0, 508) * mm, "construction": true});
            skSolve(sketch);
        }
        {
            var Q0;
            {var subQ5=sQuery(id+"F2.wireOp",EDGE,"E288");Q0=makeQuery(id+"F2.imprint","IMPRINT",FACE,{"disambiguationData":[TD([[makeQuery(id+"F2.imprint","IMPRINT",EDGE,{"derivedFrom":subQ5}),1.0]])]});}
            var Q1;
            Q1=sQuery(id+"F2.wireOp",EDGE,"E293");
            var Q2;
            Q2=sQuery(id+"F2.wireOp",EDGE,"E294");
            extrude(context, id + "F3", {"entities" : qUnion([Q0]), "operationType" : NewBodyOperationType.REMOVE, "surfaceEntities" : qUnion([Q1, Q2]), "endBound" : BoundingType.THROUGH_ALL, "oppositeDirection" : true, "depth" : 12700 * mm, "offsetDistance" : 25.4 * mm});
        }
        {
            var Q0;
            Q0=makeQuery(id+"F1.opExtrude","SWEPT_FACE",FACE,{"disambiguationData":[OSD([sQuery(id+"F0.wireOp",EDGE,"E29")])]});
            var sketch = newSketch(context, id + "F4", { "sketchPlane" : qUnion([Q0])});
            skLineSegment(sketch, "E295.0", {"start": v(304.8, 0) * mm, "end": v(-21437.6, 0) * mm});
            skLineSegment(sketch, "E296.0", {"start": v(-21437.6, 304.8) * mm, "end": v(-21437.6, 0) * mm});
            skLineSegment(sketch, "E297.0", {"start": v(304.8, 304.8) * mm, "end": v(304.8, 0) * mm});
            skPoint(sketch, "E298.orphan", {"position": v(-18338.8, 0) * mm});
            skLineSegment(sketch, "E299.0", {"start": v(304.8, 5683.25) * mm, "end": v(-21437.6, 5683.25) * mm});
            skLineSegment(sketch, "E300", {"start": v(-21437.6, 304.8) * mm, "end": v(-13369.93, 5683.25) * mm});
            skLineSegment(sketch, "E301", {"start": v(304.8, 304.8) * mm, "end": v(-7762.87, 5683.25) * mm});
            skLineSegment(sketch, "E302", {"start": v(-21437.6, 304.8) * mm, "end": v(-21132.8, 304.8) * mm, "construction": true});
            skLineSegment(sketch, "E303", {"start": v(-21132.8, 304.8) * mm, "end": v(-21132.8, 508) * mm, "construction": true});
            skLineSegment(sketch, "E304", {"start": v(-21437.6, 5683.25) * mm, "end": v(-21437.6, 304.8) * mm});
            skLineSegment(sketch, "E305", {"start": v(304.8, 5683.25) * mm, "end": v(304.8, 304.8) * mm});
            skSolve(sketch);
        }
        {
            var Q0;
            {var subQ2=sQuery(id+"F4.wireOp",EDGE,"E300");Q0=makeQuery(id+"F4.imprint","IMPRINT",FACE,{"disambiguationData":[TD([[makeQuery(id+"F4.imprint","IMPRINT",EDGE,{"derivedFrom":subQ2}),1.0]])]});}
            var Q1;
            {var subQ2=sQuery(id+"F4.wireOp",EDGE,"E301");Q1=makeQuery(id+"F4.imprint","IMPRINT",FACE,{"disambiguationData":[TD([[makeQuery(id+"F4.imprint","IMPRINT",EDGE,{"derivedFrom":subQ2}),-1.0]])]});}
            extrude(context, id + "F5", {"entities" : qUnion([Q0, Q1]), "operationType" : NewBodyOperationType.REMOVE, "endBound" : BoundingType.THROUGH_ALL, "oppositeDirection" : true, "depth" : 25.4 * mm, "offsetDistance" : 25.4 * mm});
        }
        {
            var Q0;
            Q0=qCreatedBy(makeId("Top.planeOp"),FACE);
            cPlane(context, id + "F6", {"entities" : qUnion([Q0]), "cplaneType" : CPlaneType.OFFSET, "offset" : 2743.2 * mm, "width" : 152.4 * mm, "height" : 152.4 * mm});
        }
        {
            var Q0;
            Q0=qCreatedBy(id+"F6.planeOp",FACE);
            var sketch = newSketch(context, id + "F7", { "sketchPlane" : qUnion([Q0])});
            skLineSegment(sketch, "E306.0", {"start": v(7762.88, -3892.55) * mm, "end": v(1454.15, -3892.55) * mm});
            skLineSegment(sketch, "E307.0", {"start": v(1454.15, -3892.55) * mm, "end": v(1454.15, -6623.05) * mm});
            skLineSegment(sketch, "E308.0", {"start": v(1454.15, -6623.05) * mm, "end": v(7762.88, -6623.05) * mm});
            skLineSegment(sketch, "E309.0", {"start": v(7762.88, -9201.15) * mm, "end": v(1454.15, -9201.15) * mm});
            skLineSegment(sketch, "E310.0", {"start": v(1454.15, -9201.15) * mm, "end": v(1454.15, -11931.65) * mm});
            skLineSegment(sketch, "E311.0", {"start": v(1454.15, -11931.65) * mm, "end": v(7762.88, -11931.65) * mm});
            skLineSegment(sketch, "E312.0", {"start": v(7762.88, -14509.75) * mm, "end": v(1454.15, -14509.75) * mm});
            skLineSegment(sketch, "E313.0", {"start": v(1454.15, -14509.75) * mm, "end": v(1454.15, -17240.25) * mm});
            skLineSegment(sketch, "E314.0", {"start": v(1454.15, -17240.25) * mm, "end": v(7762.88, -17240.25) * mm});
            skLineSegment(sketch, "E315.0", {"start": v(7762.87, -17392.65) * mm, "end": v(14071.6, -17392.65) * mm});
            skLineSegment(sketch, "E316.0", {"start": v(14071.6, -17392.65) * mm, "end": v(14071.6, -14814.55) * mm});
            skLineSegment(sketch, "E317.0", {"start": v(14071.6, -14814.55) * mm, "end": v(7762.88, -14814.55) * mm});
            skLineSegment(sketch, "E318.0", {"start": v(7762.88, -11931.65) * mm, "end": v(14071.6, -11931.65) * mm});
            skLineSegment(sketch, "E319.0", {"start": v(14071.6, -11931.65) * mm, "end": v(14071.6, -9201.15) * mm});
            skLineSegment(sketch, "E320.0", {"start": v(14071.6, -9201.15) * mm, "end": v(7762.88, -9201.15) * mm});
            skLineSegment(sketch, "E321.0", {"start": v(7762.88, -6318.25) * mm, "end": v(14071.6, -6318.25) * mm});
            skLineSegment(sketch, "E322.0", {"start": v(14071.6, -6318.25) * mm, "end": v(14071.6, -3740.15) * mm});
            skLineSegment(sketch, "E323.0", {"start": v(14071.6, -3740.15) * mm, "end": v(7762.87, -3740.15) * mm});
            skLineSegment(sketch, "E324", {"start": v(7762.88, -2895.6) * mm, "end": v(7762.88, -18237.2) * mm});
            skPoint(sketch, "E325.orphan", {"position": v(1454.15, -3892.55) * mm});
            skPoint(sketch, "E326.orphan", {"position": v(2895.6, -6623.05) * mm});
            skPoint(sketch, "E327.orphan", {"position": v(2895.6, -9201.15) * mm});
            skPoint(sketch, "E328.orphan", {"position": v(2895.6, -11931.65) * mm});
            skPoint(sketch, "E329.orphan", {"position": v(1454.15, -14509.75) * mm});
            skPoint(sketch, "E330.orphan", {"position": v(2895.6, -17240.25) * mm});
            skPoint(sketch, "E331.orphan", {"position": v(12630.15, -17392.65) * mm});
            skPoint(sketch, "E332.orphan", {"position": v(12630.15, -14814.55) * mm});
            skPoint(sketch, "E333.orphan", {"position": v(12630.15, -11931.65) * mm});
            skPoint(sketch, "E334.orphan", {"position": v(12630.15, -9201.15) * mm});
            skPoint(sketch, "E335.orphan", {"position": v(12630.15, -6318.25) * mm});
            skPoint(sketch, "E336.orphan", {"position": v(14071.6, -3740.15) * mm});
            skPoint(sketch, "E337.orphan", {"position": v(2895.6, -3892.55) * mm});
            skPoint(sketch, "E338.orphan", {"position": v(12630.15, -3740.15) * mm});
            skPoint(sketch, "E339.orphan", {"position": v(2895.6, -14509.75) * mm});
            skSolve(sketch);
        }
        {
            var Q0;
            Q0 = qSketchRegion(id + "F7", true);
            extrude(context, id + "F8", {"entities" : qUnion([Q0]), "operationType" : NewBodyOperationType.ADD, "oppositeDirection" : true, "depth" : 2438.4 * mm, "offsetDistance" : 25.4 * mm});
        }
        {
            var Q0;
            Q0=makeQuery(id+"F8.opExtrude","SWEPT_FACE",FACE,{"disambiguationData":[OSD([sQuery(id+"F7.wireOp",EDGE,"E316.0")])]});
            var sketch = newSketch(context, id + "F9", { "sketchPlane" : qUnion([Q0])});
            skLineSegment(sketch, "E340", {"start": v(-17545.05, 2895.6) * mm, "end": v(-16103.6, 3856.57) * mm});
            skLineSegment(sketch, "E341", {"start": v(-16103.6, 3856.57) * mm, "end": v(-14662.15, 2895.6) * mm});
            skLineSegment(sketch, "E342", {"start": v(-14662.15, 2895.6) * mm, "end": v(-14662.15, 2743.2) * mm});
            skLineSegment(sketch, "E343", {"start": v(-14662.15, 2743.2) * mm, "end": v(-17545.05, 2743.2) * mm});
            skLineSegment(sketch, "E344", {"start": v(-17545.05, 2743.2) * mm, "end": v(-17545.05, 2895.6) * mm});
            skLineSegment(sketch, "E345", {"start": v(-14662.15, 2895.6) * mm, "end": v(-14966.95, 2895.6) * mm, "construction": true});
            skLineSegment(sketch, "E346", {"start": v(-14966.95, 2895.6) * mm, "end": v(-14966.95, 3098.8) * mm, "construction": true});
            skLineSegment(sketch, "E347", {"start": v(-5029.2, 3856.57) * mm, "end": v(-6470.65, 2895.6) * mm});
            skLineSegment(sketch, "E348", {"start": v(-6470.65, 2895.6) * mm, "end": v(-6470.65, 2743.2) * mm});
            skLineSegment(sketch, "E349", {"start": v(-6470.65, 2743.2) * mm, "end": v(-3587.75, 2743.2) * mm});
            skLineSegment(sketch, "E350", {"start": v(-3587.75, 2743.2) * mm, "end": v(-3587.75, 2895.6) * mm});
            skLineSegment(sketch, "E351", {"start": v(-3587.75, 2895.6) * mm, "end": v(-5029.2, 3856.57) * mm});
            skLineSegment(sketch, "E352", {"start": v(-10566.4, 3907.37) * mm, "end": v(-12084.05, 2895.6) * mm});
            skLineSegment(sketch, "E353", {"start": v(-12084.05, 2895.6) * mm, "end": v(-12084.05, 2743.2) * mm});
            skLineSegment(sketch, "E354", {"start": v(-12084.05, 2743.2) * mm, "end": v(-9048.75, 2743.2) * mm});
            skLineSegment(sketch, "E355", {"start": v(-9048.75, 2743.2) * mm, "end": v(-9048.75, 2895.6) * mm});
            skLineSegment(sketch, "E356", {"start": v(-9048.75, 2895.6) * mm, "end": v(-10566.4, 3907.37) * mm});
            skSolve(sketch);
        }
        {
            var Q0;
            Q0=makeQuery(id+"F9.imprint","IMPRINT",FACE,{"disambiguationData":[TD([[makeQuery(id+"F9.imprint","IMPRINT",EDGE,{"derivedFrom":sQuery(id+"F9.wireOp",EDGE,"E340")}),-1.0]])]});
            var Q1;
            Q1=makeQuery(id+"F9.imprint","IMPRINT",FACE,{"disambiguationData":[TD([[makeQuery(id+"F9.imprint","IMPRINT",EDGE,{"derivedFrom":sQuery(id+"F9.wireOp",EDGE,"E352")}),1.0]])]});
            var Q2;
            Q2=makeQuery(id+"F9.imprint","IMPRINT",FACE,{"disambiguationData":[TD([[makeQuery(id+"F9.imprint","IMPRINT",EDGE,{"derivedFrom":sQuery(id+"F9.wireOp",EDGE,"E347")}),1.0]])]});
            extrude(context, id + "F10", {"entities" : qUnion([Q0, Q1, Q2]), "operationType" : NewBodyOperationType.ADD, "oppositeDirection" : true, "depth" : 3657.6 * mm, "offsetDistance" : 25.4 * mm});
        }
        {
            var Q0;
            Q0=makeQuery(id+"F10.boolean.opBoolean","MERGE",FACE,{"derivedFrom":[makeQuery(id+"F8.opExtrude","SWEPT_FACE",FACE,{"disambiguationData":[OSD([sQuery(id+"F7.wireOp",EDGE,"E316.0")])]}),makeQuery(id+"F10.opExtrude","CAP_FACE",FACE,{"disambiguationData":[OSD([sQuery(id+"F9.wireOp",EDGE,"E340"),sQuery(id+"F9.wireOp",EDGE,"E341"),sQuery(id+"F9.wireOp",EDGE,"E342"),sQuery(id+"F9.wireOp",EDGE,"E343"),sQuery(id+"F9.wireOp",EDGE,"E344")])],"isStart":true})]});
            var sketch = newSketch(context, id + "F11", { "sketchPlane" : qUnion([Q0])});
            skLineSegment(sketch, "E357", {"start": v(-17392.65, 2743.2) * mm, "end": v(-17392.65, 2814.04) * mm});
            skLineSegment(sketch, "E358", {"start": v(-17392.65, 2814.04) * mm, "end": v(-16103.6, 3673.4) * mm});
            skLineSegment(sketch, "E359", {"start": v(-16103.6, 3673.4) * mm, "end": v(-14814.55, 2814.04) * mm});
            skLineSegment(sketch, "E360", {"start": v(-14814.55, 2814.04) * mm, "end": v(-14814.55, 2743.2) * mm});
            skLineSegment(sketch, "E361.0", {"start": v(-16103.6, 3856.57) * mm, "end": v(-14662.15, 2895.6) * mm});
            skLineSegment(sketch, "E362.0", {"start": v(-17545.05, 2895.6) * mm, "end": v(-16103.6, 3856.57) * mm});
            skLineSegment(sketch, "E363.0", {"start": v(-17545.05, 2743.2) * mm, "end": v(-17545.05, 2895.6) * mm});
            skLineSegment(sketch, "E364.0", {"start": v(-17392.65, 2743.2) * mm, "end": v(-17545.05, 2743.2) * mm});
            skLineSegment(sketch, "E365.0", {"start": v(-14662.15, 2743.2) * mm, "end": v(-14814.55, 2743.2) * mm});
            skLineSegment(sketch, "E366.0", {"start": v(-10566.4, 3907.37) * mm, "end": v(-12084.05, 2895.6) * mm});
            skLineSegment(sketch, "E367.0", {"start": v(-9048.75, 2895.6) * mm, "end": v(-10566.4, 3907.37) * mm});
            skLineSegment(sketch, "E368.0", {"start": v(-9048.75, 2743.2) * mm, "end": v(-9048.75, 2895.6) * mm});
            skLineSegment(sketch, "E369.0", {"start": v(-9201.15, 2743.2) * mm, "end": v(-9048.75, 2743.2) * mm});
            skLineSegment(sketch, "E370.0", {"start": v(-12084.05, 2895.6) * mm, "end": v(-12084.05, 2743.2) * mm});
            skLineSegment(sketch, "E371.0", {"start": v(-12084.05, 2743.2) * mm, "end": v(-11931.65, 2743.2) * mm});
            skLineSegment(sketch, "E372", {"start": v(-11931.65, 2743.2) * mm, "end": v(-11931.65, 2814.04) * mm});
            skLineSegment(sketch, "E373", {"start": v(-11931.65, 2814.04) * mm, "end": v(-10566.4, 3724.2) * mm});
            skLineSegment(sketch, "E374", {"start": v(-10566.4, 3724.2) * mm, "end": v(-9201.15, 2814.04) * mm});
            skLineSegment(sketch, "E375", {"start": v(-9201.15, 2814.04) * mm, "end": v(-9201.15, 2743.2) * mm});
            skLineSegment(sketch, "E376.0", {"start": v(-5029.2, 3856.57) * mm, "end": v(-6470.65, 2895.6) * mm});
            skLineSegment(sketch, "E377.0", {"start": v(-6470.65, 2895.6) * mm, "end": v(-6470.65, 2743.2) * mm});
            skLineSegment(sketch, "E378.0", {"start": v(-6470.65, 2743.2) * mm, "end": v(-6318.25, 2743.2) * mm});
            skLineSegment(sketch, "E379.0", {"start": v(-3740.15, 2743.2) * mm, "end": v(-3587.75, 2743.2) * mm});
            skLineSegment(sketch, "E380.0", {"start": v(-3587.75, 2743.2) * mm, "end": v(-3587.75, 2895.6) * mm});
            skLineSegment(sketch, "E381.0", {"start": v(-3587.75, 2895.6) * mm, "end": v(-5029.2, 3856.57) * mm});
            skLineSegment(sketch, "E382", {"start": v(-6318.25, 2743.2) * mm, "end": v(-6318.25, 2814.04) * mm});
            skLineSegment(sketch, "E383", {"start": v(-6318.25, 2814.04) * mm, "end": v(-5029.2, 3673.4) * mm});
            skLineSegment(sketch, "E384", {"start": v(-5029.2, 3673.4) * mm, "end": v(-3740.15, 2814.04) * mm});
            skLineSegment(sketch, "E385", {"start": v(-3740.15, 2814.04) * mm, "end": v(-3740.15, 2743.2) * mm});
            skSolve(sketch);
        }
        {
            var Q0;
            Q0 = qSketchRegion(id + "F11", true);
            var Q1;
            Q1=makeQuery(id+"F11.imprint","IMPRINT",FACE,{"disambiguationData":[TD([[makeQuery(id+"F11.imprint","IMPRINT",EDGE,{"derivedFrom":sQuery(id+"F11.wireOp",EDGE,"E357")}),1.0]])]});
            extrude(context, id + "F12", {"entities" : qUnion([Q0, Q1]), "operationType" : NewBodyOperationType.ADD, "depth" : 152.4 * mm, "offsetDistance" : 25.4 * mm});
        }
        {
            var Q0;
            Q0=makeQuery(id+"F10.boolean.opBoolean","MERGE",FACE,{"derivedFrom":[makeQuery(id+"F8.opExtrude","SWEPT_FACE",FACE,{"disambiguationData":[OSD([sQuery(id+"F7.wireOp",EDGE,"E316.0")])]}),makeQuery(id+"F10.opExtrude","CAP_FACE",FACE,{"disambiguationData":[OSD([sQuery(id+"F9.wireOp",EDGE,"E340"),sQuery(id+"F9.wireOp",EDGE,"E341"),sQuery(id+"F9.wireOp",EDGE,"E342"),sQuery(id+"F9.wireOp",EDGE,"E343"),sQuery(id+"F9.wireOp",EDGE,"E344")])],"isStart":true})]});
            var sketch = newSketch(context, id + "F13", { "sketchPlane" : qUnion([Q0])});
            skLineSegment(sketch, "E386", {"start": v(-17392.65, 2743.2) * mm, "end": v(-14814.55, 2743.2) * mm, "construction": true});
            skLineSegment(sketch, "E387", {"start": v(-16103.6, 2743.2) * mm, "end": v(-16103.6, 1477.43) * mm, "construction": true});
            skLineSegment(sketch, "E388.bottom", {"start": v(-16560.8, 2794) * mm, "end": v(-15646.4, 2794) * mm});
            skLineSegment(sketch, "E388.top", {"start": v(-16560.8, 1574.8) * mm, "end": v(-15646.4, 1574.8) * mm});
            skLineSegment(sketch, "E388.left", {"start": v(-16560.8, 2794) * mm, "end": v(-16560.8, 1574.8) * mm});
            skLineSegment(sketch, "E388.right", {"start": v(-15646.4, 2794) * mm, "end": v(-15646.4, 1574.8) * mm});
            skPoint(sketch, "E389", {"position": v(-16103.6, 2794) * mm});
            skLineSegment(sketch, "E390.0", {"start": v(-12084.05, 2743.2) * mm, "end": v(-11931.65, 2743.2) * mm, "construction": true});
            skLineSegment(sketch, "E391.0", {"start": v(-9201.15, 2743.2) * mm, "end": v(-9048.75, 2743.2) * mm, "construction": true});
            skLineSegment(sketch, "E392.0", {"start": v(-9201.15, 1477.43) * mm, "end": v(-11931.65, 1477.43) * mm, "construction": true});
            skLineSegment(sketch, "E393.0", {"start": v(-3740.15, 1477.43) * mm, "end": v(-6318.25, 1477.43) * mm, "construction": true});
            skLineSegment(sketch, "E394.0", {"start": v(-6470.65, 2743.2) * mm, "end": v(-6318.25, 2743.2) * mm, "construction": true});
            skLineSegment(sketch, "E395.0", {"start": v(-3740.15, 2743.2) * mm, "end": v(-3587.75, 2743.2) * mm, "construction": true});
            skLineSegment(sketch, "E396", {"start": v(-11931.65, 2743.2) * mm, "end": v(-9201.15, 2743.2) * mm, "construction": true});
            skLineSegment(sketch, "E397", {"start": v(-6318.25, 2743.2) * mm, "end": v(-3740.15, 2743.2) * mm, "construction": true});
            skLineSegment(sketch, "E398", {"start": v(-10566.4, 2743.2) * mm, "end": v(-10566.4, 1477.43) * mm, "construction": true});
            skLineSegment(sketch, "E399", {"start": v(-5029.2, 2743.2) * mm, "end": v(-5029.2, 1477.43) * mm, "construction": true});
            skLineSegment(sketch, "E400.bottom", {"start": v(-11023.6, 2794) * mm, "end": v(-10109.2, 2794) * mm});
            skLineSegment(sketch, "E400.top", {"start": v(-11023.6, 1574.8) * mm, "end": v(-10109.2, 1574.8) * mm});
            skLineSegment(sketch, "E400.left", {"start": v(-11023.6, 2794) * mm, "end": v(-11023.6, 1574.8) * mm});
            skLineSegment(sketch, "E400.right", {"start": v(-10109.2, 2794) * mm, "end": v(-10109.2, 1574.8) * mm});
            skLineSegment(sketch, "E401.bottom", {"start": v(-5486.4, 2794) * mm, "end": v(-4572, 2794) * mm});
            skLineSegment(sketch, "E401.top", {"start": v(-5486.4, 1574.8) * mm, "end": v(-4572, 1574.8) * mm});
            skLineSegment(sketch, "E401.left", {"start": v(-5486.4, 2794) * mm, "end": v(-5486.4, 1574.8) * mm});
            skLineSegment(sketch, "E401.right", {"start": v(-4572, 2794) * mm, "end": v(-4572, 1574.8) * mm});
            skPoint(sketch, "E402", {"position": v(-10566.4, 1574.8) * mm});
            skPoint(sketch, "E403", {"position": v(-5029.2, 1574.8) * mm});
            skSolve(sketch);
        }
        {
            var Q0;
            Q0 = qSketchRegion(id + "F13", true);
            extrude(context, id + "F14", {"entities" : qUnion([Q0]), "operationType" : NewBodyOperationType.REMOVE, "oppositeDirection" : true, "depth" : 76.2 * mm, "offsetDistance" : 25.4 * mm});
        }
    });
